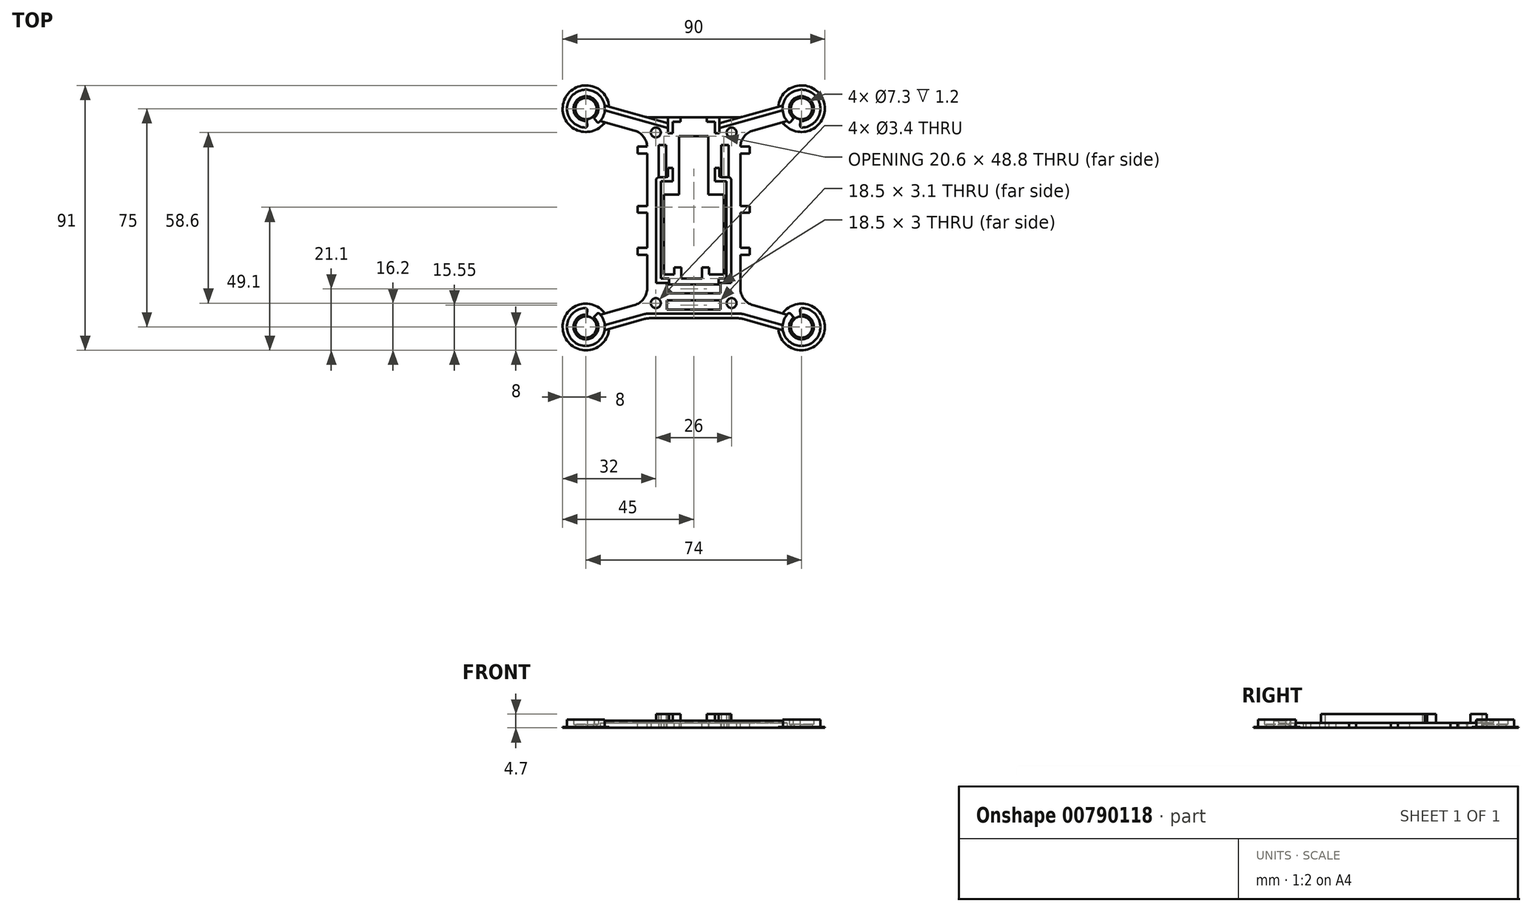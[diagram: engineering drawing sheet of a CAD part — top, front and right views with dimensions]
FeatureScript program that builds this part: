
annotation { "Feature Type Name" : "Feature", "Feature Type Description" : "" }
export const myFeature = defineFeature(function(context is Context, id is Id, definition is map)
    precondition{}
    {
        {
            var Q0;
            Q0=qCreatedBy(makeId("Top.planeOp"),FACE);
            var sketch = newSketch(context, id + "F0", { "sketchPlane" : qUnion([Q0])});
            skCircle(sketch, "E0", {"center": v(-37, 37.5) * mm, "radius": 32.5 * mm, "construction": true});
            skCircle(sketch, "E1.MirrorC", {"center": v(37, 37.5) * mm, "radius": 32.5 * mm, "construction": true});
            skCircle(sketch, "E2.MirrorC", {"center": v(37, -37.5) * mm, "radius": 32.5 * mm, "construction": true});
            skCircle(sketch, "E3.MirrorC", {"center": v(-37, -37.5) * mm, "radius": 32.5 * mm, "construction": true});
            skLineSegment(sketch, "E4.bottom", {"start": v(-37, 37.5) * mm, "end": v(37, 37.5) * mm, "construction": true});
            skLineSegment(sketch, "E4.top", {"start": v(-37, -37.5) * mm, "end": v(37, -37.5) * mm, "construction": true});
            skLineSegment(sketch, "E4.left", {"start": v(-37, 37.5) * mm, "end": v(-37, -37.5) * mm, "construction": true});
            skLineSegment(sketch, "E4.right", {"start": v(37, 37.5) * mm, "end": v(37, -37.5) * mm, "construction": true});
            skLineSegment(sketch, "E5", {"start": v(-37, 37.5) * mm, "end": v(0, 0) * mm, "construction": true});
            skCircle(sketch, "E6", {"center": v(-37, 37.5) * mm, "radius": 3.65 * mm});
            skCircle(sketch, "E7.MirrorC", {"center": v(37, 37.5) * mm, "radius": 3.65 * mm});
            skCircle(sketch, "E8.MirrorC", {"center": v(37, -37.5) * mm, "radius": 3.65 * mm});
            skCircle(sketch, "E9.MirrorC", {"center": v(-37, -37.5) * mm, "radius": 3.65 * mm});
            skArc(sketch, "E10", {"start": v(-30.59, 38.57) * mm, "mid": v(-43.26, 39.25) * mm, "end": v(-32.07, 33.27) * mm});
            skArc(sketch, "E11.MirrorC", {"start": v(30.59, 38.57) * mm, "mid": v(43.26, 39.25) * mm, "end": v(32.07, 33.27) * mm});
            skArc(sketch, "E12.MirrorC", {"start": v(-30.59, -38.57) * mm, "mid": v(-43.26, -39.25) * mm, "end": v(-32.07, -33.27) * mm});
            skArc(sketch, "E13.MirrorC", {"start": v(30.59, -38.57) * mm, "mid": v(43.26, -39.25) * mm, "end": v(32.07, -33.27) * mm});
            skLineSegment(sketch, "E14.bottom", {"start": v(-10.3, 11) * mm, "end": v(-5, 11) * mm, "construction": true});
            skLineSegment(sketch, "E14.top", {"start": v(-10.3, -20.5) * mm, "end": v(10.3, -20.5) * mm});
            skLineSegment(sketch, "E14.right", {"start": v(10.3, 8) * mm, "end": v(10.3, -20.5) * mm});
            skPoint(sketch, "E14.middle", {"position": v(0, -4.75) * mm});
            skLineSegment(sketch, "E15.top", {"start": v(-5, 28) * mm, "end": v(5, 28) * mm});
            skLineSegment(sketch, "E15.left", {"start": v(-5, 11) * mm, "end": v(-5, 16) * mm});
            skLineSegment(sketch, "E15.right", {"start": v(5, 11) * mm, "end": v(5, 16) * mm});
            skPoint(sketch, "E15.middle", {"position": v(0, 19.5) * mm});
            skPoint(sketch, "E15.middle.positionSnap0", {"position": v(0, 11) * mm});
            skPoint(sketch, "E15.centerSnap0", {"position": v(0, 11) * mm});
            skLineSegment(sketch, "E16.trimOffspring", {"start": v(5, 11) * mm, "end": v(10.3, 11) * mm, "construction": true});
            skLineSegment(sketch, "E17.bottom", {"start": v(-16, 34.5) * mm, "end": v(16, 34.5) * mm});
            skLineSegment(sketch, "E17.top", {"start": v(-16, -34.5) * mm, "end": v(16, -34.5) * mm});
            skLineSegment(sketch, "E17.left", {"start": v(-16, 28.8) * mm, "end": v(-16, -28.8) * mm});
            skLineSegment(sketch, "E17.right", {"start": v(16, 28.8) * mm, "end": v(16, -28.8) * mm});
            skPoint(sketch, "E17.middle", {"position": v(0, 0) * mm});
            skLineSegment(sketch, "E18", {"start": v(-30.59, 38.57) * mm, "end": v(-16, 34.5) * mm});
            skLineSegment(sketch, "E19", {"start": v(-32.07, 33.27) * mm, "end": v(-16, 28.8) * mm});
            skLineSegment(sketch, "E20", {"start": v(-37, 37.5) * mm, "end": v(-17.81, 32.15) * mm, "construction": true});
            skLineSegment(sketch, "E21.MirrorCS", {"start": v(30.59, 38.57) * mm, "end": v(16, 34.5) * mm});
            skLineSegment(sketch, "E22.MirrorCS", {"start": v(32.07, 33.27) * mm, "end": v(16, 28.8) * mm});
            skLineSegment(sketch, "E23.MirrorCS", {"start": v(-30.59, -38.57) * mm, "end": v(-16, -34.5) * mm});
            skLineSegment(sketch, "E24.MirrorCS", {"start": v(-32.07, -33.27) * mm, "end": v(-16, -28.8) * mm});
            skLineSegment(sketch, "E25.MirrorCS", {"start": v(30.59, -38.57) * mm, "end": v(16, -34.5) * mm});
            skLineSegment(sketch, "E26.MirrorCS", {"start": v(32.07, -33.27) * mm, "end": v(16, -28.8) * mm});
            skLineSegment(sketch, "E27.bottom", {"start": v(-11.3, 11.8) * mm, "end": v(11.3, 11.8) * mm, "construction": true});
            skLineSegment(sketch, "E27.top", {"start": v(-11.3, -21.3) * mm, "end": v(11.3, -21.3) * mm, "construction": true});
            skLineSegment(sketch, "E27.left", {"start": v(-11.3, 11.8) * mm, "end": v(-11.3, -21.3) * mm, "construction": true});
            skLineSegment(sketch, "E27.right", {"start": v(11.3, 11.8) * mm, "end": v(11.3, -21.3) * mm, "construction": true});
            skLineSegment(sketch, "E28.bottom", {"start": v(-9.25, -22.9) * mm, "end": v(9.25, -22.9) * mm});
            skLineSegment(sketch, "E28.top", {"start": v(-9.25, -25.9) * mm, "end": v(9.25, -25.9) * mm});
            skLineSegment(sketch, "E28.left", {"start": v(-9.25, -22.9) * mm, "end": v(-9.25, -25.9) * mm});
            skLineSegment(sketch, "E28.right", {"start": v(9.25, -22.9) * mm, "end": v(9.25, -25.9) * mm});
            skPoint(sketch, "E28.middle", {"position": v(0, -24.4) * mm});
            skLineSegment(sketch, "E29.bottom", {"start": v(-9.25, -28.4) * mm, "end": v(9.25, -28.4) * mm});
            skLineSegment(sketch, "E29.top", {"start": v(-9.25, -31.5) * mm, "end": v(9.25, -31.5) * mm});
            skLineSegment(sketch, "E29.left", {"start": v(-9.25, -28.4) * mm, "end": v(-9.25, -31.5) * mm});
            skLineSegment(sketch, "E29.right", {"start": v(9.25, -28.4) * mm, "end": v(9.25, -31.5) * mm});
            skPoint(sketch, "E29.middle", {"position": v(0, -29.95) * mm});
            skCircle(sketch, "E30", {"center": v(-13, 29.3) * mm, "radius": 1.7 * mm});
            skCircle(sketch, "E31.MirrorC", {"center": v(13, 29.3) * mm, "radius": 1.7 * mm});
            skCircle(sketch, "E32.MirrorC", {"center": v(-13, -29.3) * mm, "radius": 1.7 * mm});
            skCircle(sketch, "E33.MirrorC", {"center": v(13, -29.3) * mm, "radius": 1.7 * mm});
            skLineSegment(sketch, "E34.bottom", {"start": v(-12, 25) * mm, "end": v(-9.5, 25) * mm});
            skLineSegment(sketch, "E34.top", {"start": v(-12, 14) * mm, "end": v(-9.5, 14) * mm});
            skLineSegment(sketch, "E34.left", {"start": v(-12, 25) * mm, "end": v(-12, 14) * mm});
            skLineSegment(sketch, "E34.right", {"start": v(-9.5, 25) * mm, "end": v(-9.5, 14) * mm});
            skPoint(sketch, "E34.middle", {"position": v(-10.75, 19.5) * mm});
            skLineSegment(sketch, "E35.MirrorCS", {"start": v(12, 25) * mm, "end": v(9.5, 25) * mm});
            skLineSegment(sketch, "E36.MirrorCS", {"start": v(12, 25) * mm, "end": v(12, 14) * mm});
            skLineSegment(sketch, "E37.MirrorCS", {"start": v(12, 14) * mm, "end": v(9.5, 14) * mm});
            skLineSegment(sketch, "E38.MirrorCS", {"start": v(9.5, 25) * mm, "end": v(9.5, 14) * mm});
            skLineSegment(sketch, "E39.trimOffspring", {"start": v(-5, 16) * mm, "end": v(-5, 28) * mm});
            skLineSegment(sketch, "E40.trimOffspring", {"start": v(5, 16) * mm, "end": v(5, 28) * mm});
            skLineSegment(sketch, "E41", {"start": v(-10.3, 8) * mm, "end": v(-5, 8) * mm});
            skLineSegment(sketch, "E42", {"start": v(-5, 8) * mm, "end": v(-5, 11) * mm});
            skLineSegment(sketch, "E43.trimOffspring", {"start": v(-10.3, 8) * mm, "end": v(-10.3, -20.5) * mm});
            skLineSegment(sketch, "E44.MirrorCS", {"start": v(5, 8) * mm, "end": v(5, 11) * mm});
            skLineSegment(sketch, "E45.MirrorCS", {"start": v(10.3, 8) * mm, "end": v(5, 8) * mm});
            skSolve(sketch);
        }
        {
            var Q0;
            Q0=makeQuery(id+"F0.imprint","IMPRINT",FACE,{"disambiguationData":[TD([[makeQuery(id+"F0.imprint","IMPRINT",EDGE,{"derivedFrom":sQuery(id+"F0.wireOp",EDGE,"E6")}),-1.0]])]});
            extrude(context, id + "F1", {"entities" : qUnion([Q0]), "depth" : 1.7 * mm, "offsetDistance" : 25 * mm});
        }
        {
            var Q0;
            Q0=makeQuery(id+"F1.opExtrude","CAP_FACE",FACE,{"disambiguationData":[OSD([sQuery(id+"F0.wireOp",EDGE,"E6"),sQuery(id+"F0.wireOp",EDGE,"E7.MirrorC"),sQuery(id+"F0.wireOp",EDGE,"E8.MirrorC"),sQuery(id+"F0.wireOp",EDGE,"E9.MirrorC"),sQuery(id+"F0.wireOp",EDGE,"E10"),sQuery(id+"F0.wireOp",EDGE,"E11.MirrorC"),sQuery(id+"F0.wireOp",EDGE,"E12.MirrorC"),sQuery(id+"F0.wireOp",EDGE,"E13.MirrorC"),sQuery(id+"F0.wireOp",EDGE,"E14.bottom"),sQuery(id+"F0.wireOp",EDGE,"E14.top"),sQuery(id+"F0.wireOp",EDGE,"E14.left"),sQuery(id+"F0.wireOp",EDGE,"E14.right"),sQuery(id+"F0.wireOp",EDGE,"E15.top"),sQuery(id+"F0.wireOp",EDGE,"E15.left"),sQuery(id+"F0.wireOp",EDGE,"E15.right"),sQuery(id+"F0.wireOp",EDGE,"E16.trimOffspring"),sQuery(id+"F0.wireOp",EDGE,"E17.bottom"),sQuery(id+"F0.wireOp",EDGE,"E17.top"),sQuery(id+"F0.wireOp",EDGE,"E17.left"),sQuery(id+"F0.wireOp",EDGE,"E17.right"),sQuery(id+"F0.wireOp",EDGE,"E18"),sQuery(id+"F0.wireOp",EDGE,"E19"),sQuery(id+"F0.wireOp",EDGE,"E21.MirrorCS"),sQuery(id+"F0.wireOp",EDGE,"E22.MirrorCS"),sQuery(id+"F0.wireOp",EDGE,"E23.MirrorCS"),sQuery(id+"F0.wireOp",EDGE,"E24.MirrorCS"),sQuery(id+"F0.wireOp",EDGE,"E25.MirrorCS"),sQuery(id+"F0.wireOp",EDGE,"E26.MirrorCS")])],"isStart":false});
            var sketch = newSketch(context, id + "F2", { "sketchPlane" : qUnion([Q0])});
            skLineSegment(sketch, "E46.bottom", {"start": v(-11.25, 12.5) * mm, "end": v(-7.25, 12.5) * mm});
            skLineSegment(sketch, "E46.top", {"start": v(-11.25, -20.8) * mm, "end": v(11.25, -20.8) * mm});
            skLineSegment(sketch, "E46.left", {"start": v(-11.25, 12.5) * mm, "end": v(-11.25, -20.8) * mm});
            skLineSegment(sketch, "E46.right", {"start": v(11.25, 12.5) * mm, "end": v(11.25, -20.8) * mm});
            skPoint(sketch, "E46.middle", {"position": v(0, -4.15) * mm});
            skLineSegment(sketch, "E47.bottom", {"start": v(-12.85, 14.1) * mm, "end": v(-8.85, 14.1) * mm});
            skLineSegment(sketch, "E47.top", {"start": v(-12.85, -22.4) * mm, "end": v(12.85, -22.4) * mm});
            skLineSegment(sketch, "E47.left", {"start": v(-12.85, 14.1) * mm, "end": v(-12.85, -22.4) * mm});
            skLineSegment(sketch, "E47.right", {"start": v(12.85, 14.1) * mm, "end": v(12.85, -22.4) * mm});
            skLineSegment(sketch, "E48", {"start": v(-7.25, 14.1) * mm, "end": v(-7.25, 33) * mm});
            skLineSegment(sketch, "E49", {"start": v(-7.25, 33) * mm, "end": v(7.25, 33) * mm});
            skLineSegment(sketch, "E50", {"start": v(7.25, 33) * mm, "end": v(7.25, 14.1) * mm});
            skLineSegment(sketch, "E51", {"start": v(-8.85, 14.1) * mm, "end": v(-8.85, 34.6) * mm});
            skLineSegment(sketch, "E52", {"start": v(-8.85, 34.6) * mm, "end": v(8.85, 34.6) * mm});
            skLineSegment(sketch, "E53", {"start": v(8.85, 34.6) * mm, "end": v(8.85, 14.1) * mm});
            skLineSegment(sketch, "E54.trimOffspring", {"start": v(8.85, 14.1) * mm, "end": v(12.85, 14.1) * mm});
            skLineSegment(sketch, "E55", {"start": v(-7.25, 14.1) * mm, "end": v(-7.25, 12.5) * mm});
            skLineSegment(sketch, "E56", {"start": v(7.25, 14.1) * mm, "end": v(7.25, 12.5) * mm});
            skLineSegment(sketch, "E57.trimOffspring", {"start": v(7.25, 12.5) * mm, "end": v(11.25, 12.5) * mm});
            skSolve(sketch);
        }
        {
            var Q0;
            Q0=makeQuery(id+"F2.imprint","IMPRINT",FACE,{"disambiguationData":[TD([[makeQuery(id+"F2.imprint","IMPRINT",EDGE,{"derivedFrom":sQuery(id+"F2.wireOp",EDGE,"E46.bottom")}),1.0]])]});
            extrude(context, id + "F3", {"entities" : qUnion([Q0]), "operationType" : NewBodyOperationType.ADD, "depth" : 3 * mm, "offsetDistance" : 25 * mm});
        }
        {
            var Q0;
            Q0=makeQuery(id+"F3.opExtrude","SWEPT_EDGE",EDGE,{"disambiguationData":[OSD([sQuery(id+"F2.wireOp",EDGE,"E47.bottom"),sQuery(id+"F2.wireOp",EDGE,"E47.left")])]});
            var Q1;
            Q1=makeQuery(id+"F3.opExtrude","SWEPT_EDGE",EDGE,{"disambiguationData":[OSD([sQuery(id+"F2.wireOp",EDGE,"E47.right"),sQuery(id+"F2.wireOp",EDGE,"E54.trimOffspring")])]});
            chamfer(context, id + "F4", {"entities" : qUnion([Q0, Q1]), "width" : 0.8 * mm, "tangentPropagation" : true});
        }
        {
            var Q0;
            Q0=makeQuery(id+"F3.opExtrude","CAP_FACE",FACE,{"disambiguationData":[OSD([sQuery(id+"F2.wireOp",EDGE,"E46.bottom"),sQuery(id+"F2.wireOp",EDGE,"E46.top"),sQuery(id+"F2.wireOp",EDGE,"E46.left"),sQuery(id+"F2.wireOp",EDGE,"E46.right"),sQuery(id+"F2.wireOp",EDGE,"E47.bottom"),sQuery(id+"F2.wireOp",EDGE,"E47.top"),sQuery(id+"F2.wireOp",EDGE,"E47.left"),sQuery(id+"F2.wireOp",EDGE,"E47.right"),sQuery(id+"F2.wireOp",EDGE,"E48"),sQuery(id+"F2.wireOp",EDGE,"E49"),sQuery(id+"F2.wireOp",EDGE,"E50"),sQuery(id+"F2.wireOp",EDGE,"E51"),sQuery(id+"F2.wireOp",EDGE,"E52"),sQuery(id+"F2.wireOp",EDGE,"E53"),sQuery(id+"F2.wireOp",EDGE,"E54.trimOffspring"),sQuery(id+"F2.wireOp",EDGE,"E55"),sQuery(id+"F2.wireOp",EDGE,"E56"),sQuery(id+"F2.wireOp",EDGE,"E57.trimOffspring")])],"isStart":false});
            var sketch = newSketch(context, id + "F5", { "sketchPlane" : qUnion([Q0])});
            skLineSegment(sketch, "E58.bottom", {"start": v(-4.5, 34.5) * mm, "end": v(4.5, 34.5) * mm});
            skLineSegment(sketch, "E58.top", {"start": v(-4.5, 33) * mm, "end": v(4.5, 33) * mm});
            skLineSegment(sketch, "E58.left", {"start": v(-4.5, 34.5) * mm, "end": v(-4.5, 33) * mm});
            skLineSegment(sketch, "E58.right", {"start": v(4.5, 34.5) * mm, "end": v(4.5, 33) * mm});
            skPoint(sketch, "E58.middle", {"position": v(0, 33.75) * mm});
            skLineSegment(sketch, "E59.bottom", {"start": v(-8.5, -20.8) * mm, "end": v(8.5, -20.8) * mm});
            skLineSegment(sketch, "E59.top", {"start": v(-8.5, -22.4) * mm, "end": v(8.5, -22.4) * mm});
            skLineSegment(sketch, "E59.left", {"start": v(-8.5, -20.8) * mm, "end": v(-8.5, -22.4) * mm});
            skLineSegment(sketch, "E59.right", {"start": v(8.5, -20.8) * mm, "end": v(8.5, -22.4) * mm});
            skPoint(sketch, "E59.middle", {"position": v(0, -21.6) * mm});
            skLineSegment(sketch, "E60.bottom", {"start": v(-8.85, 29) * mm, "end": v(-7.25, 29) * mm});
            skLineSegment(sketch, "E60.top", {"start": v(-8.85, 17.1) * mm, "end": v(-7.25, 17.1) * mm});
            skLineSegment(sketch, "E60.left", {"start": v(-8.85, 29) * mm, "end": v(-8.85, 17.1) * mm});
            skLineSegment(sketch, "E60.right", {"start": v(-7.25, 29) * mm, "end": v(-7.25, 17.1) * mm});
            skLineSegment(sketch, "E61.MirrorCS", {"start": v(8.85, 29) * mm, "end": v(7.25, 29) * mm});
            skLineSegment(sketch, "E62.MirrorCS", {"start": v(8.85, 17.1) * mm, "end": v(7.25, 17.1) * mm});
            skLineSegment(sketch, "E63.MirrorCS", {"start": v(7.25, 29) * mm, "end": v(7.25, 17.1) * mm});
            skLineSegment(sketch, "E64.MirrorCS", {"start": v(8.85, 29) * mm, "end": v(8.85, 17.1) * mm});
            skSolve(sketch);
        }
        {
            var Q0;
            Q0 = qSketchRegion(id + "F5", true);
            var Q1;
            {var subQ0=sQuery(id+"F0.wireOp",EDGE,"E38.MirrorCS");var subQ1=sQuery(id+"F0.wireOp",EDGE,"E37.MirrorCS");var subQ2=sQuery(id+"F0.wireOp",EDGE,"E36.MirrorCS");var subQ3=sQuery(id+"F0.wireOp",EDGE,"E35.MirrorCS");var subQ4=sQuery(id+"F0.wireOp",EDGE,"E29.top");var subQ5=sQuery(id+"F0.wireOp",EDGE,"E34.right");var subQ6=sQuery(id+"F0.wireOp",EDGE,"E29.bottom");var subQ7=sQuery(id+"F0.wireOp",EDGE,"E34.left");var subQ8=sQuery(id+"F0.wireOp",EDGE,"E34.top");var subQ9=sQuery(id+"F0.wireOp",EDGE,"E34.bottom");var subQ10=sQuery(id+"F0.wireOp",EDGE,"E33.MirrorC");var subQ11=sQuery(id+"F0.wireOp",EDGE,"E28.bottom");var subQ12=sQuery(id+"F0.wireOp",EDGE,"E32.MirrorC");var subQ13=sQuery(id+"F0.wireOp",EDGE,"E26.MirrorCS");var subQ14=sQuery(id+"F0.wireOp",EDGE,"E31.MirrorC");var subQ15=sQuery(id+"F0.wireOp",EDGE,"E25.MirrorCS");var subQ16=sQuery(id+"F0.wireOp",EDGE,"E30");var subQ17=sQuery(id+"F0.wireOp",EDGE,"E24.MirrorCS");var subQ18=sQuery(id+"F0.wireOp",EDGE,"E29.right");var subQ19=sQuery(id+"F0.wireOp",EDGE,"E29.left");var subQ20=sQuery(id+"F0.wireOp",EDGE,"E28.right");var subQ21=sQuery(id+"F0.wireOp",EDGE,"E28.left");var subQ22=sQuery(id+"F0.wireOp",EDGE,"E13.MirrorC");var subQ23=sQuery(id+"F0.wireOp",EDGE,"E12.MirrorC");var subQ24=sQuery(id+"F0.wireOp",EDGE,"E11.MirrorC");var subQ25=sQuery(id+"F0.wireOp",EDGE,"E10");var subQ26=sQuery(id+"F0.wireOp",EDGE,"E6");var subQ27=sQuery(id+"F0.wireOp",EDGE,"E23.MirrorCS");var subQ28=sQuery(id+"F0.wireOp",EDGE,"E17.top");var subQ29=sQuery(id+"F0.wireOp",EDGE,"E9.MirrorC");var subQ30=sQuery(id+"F0.wireOp",EDGE,"E28.top");var subQ31=sQuery(id+"F0.wireOp",EDGE,"E7.MirrorC");var subQ32=sQuery(id+"F0.wireOp",EDGE,"E17.bottom");var subQ33=sQuery(id+"F0.wireOp",EDGE,"E8.MirrorC");var subQ34=sQuery(id+"F0.wireOp",EDGE,"E17.left");var subQ35=sQuery(id+"F0.wireOp",EDGE,"E17.right");var subQ36=sQuery(id+"F0.wireOp",EDGE,"E18");var subQ37=sQuery(id+"F0.wireOp",EDGE,"E19");var subQ38=sQuery(id+"F0.wireOp",EDGE,"E21.MirrorCS");var subQ39=sQuery(id+"F0.wireOp",EDGE,"E22.MirrorCS");Q1=makeQuery(id+"F3.boolean.opBoolean","SPLIT",FACE,{"disambiguationData":[TD([makeQuery(id+"F1.opExtrude","SWEPT_FACE",FACE,{"disambiguationData":[OSD([subQ26])]})])],"derivedFrom":makeQuery(id+"F1.opExtrude","CAP_FACE",FACE,{"disambiguationData":[OSD([subQ26,subQ31,subQ33,subQ29,subQ25,subQ24,subQ23,subQ22,sQuery(id+"F0.wireOp",EDGE,"E14.top"),sQuery(id+"F0.wireOp",EDGE,"E14.right"),sQuery(id+"F0.wireOp",EDGE,"E15.top"),sQuery(id+"F0.wireOp",EDGE,"E15.left"),sQuery(id+"F0.wireOp",EDGE,"E15.right"),subQ32,subQ28,subQ34,subQ35,subQ36,subQ37,subQ38,subQ39,subQ27,subQ17,subQ15,subQ13,subQ11,subQ30,subQ21,subQ20,subQ6,subQ4,subQ19,subQ18,subQ16,subQ14,subQ12,subQ10,subQ9,subQ8,subQ7,subQ5,subQ3,subQ2,subQ1,subQ0,sQuery(id+"F0.wireOp",EDGE,"E39.trimOffspring"),sQuery(id+"F0.wireOp",EDGE,"E40.trimOffspring"),sQuery(id+"F0.wireOp",EDGE,"E41"),sQuery(id+"F0.wireOp",EDGE,"E42"),sQuery(id+"F0.wireOp",EDGE,"E43.trimOffspring"),sQuery(id+"F0.wireOp",EDGE,"E44.MirrorCS"),sQuery(id+"F0.wireOp",EDGE,"E45.MirrorCS")])],"isStart":false})});}
            extrude(context, id + "F6", {"entities" : qUnion([Q0]), "operationType" : NewBodyOperationType.REMOVE, "endBound" : BoundingType.UP_TO_SURFACE, "oppositeDirection" : true, "depth" : 25 * mm, "endBoundEntityFace" : qUnion([Q1]), "offsetDistance" : 25 * mm});
        }
        {
            var Q0;
            {var subQ26=sQuery(id+"F0.wireOp",EDGE,"E14.top");Q0=makeQuery(id+"FuSGAjuN3hY24FW_1.boolean.opBoolean","SPLIT",FACE,{"disambiguationData":[TD([makeQuery(id+"FuSGAjuN3hY24FW_1.opExtrude","SWEPT_FACE",FACE,{"disambiguationData":[OSD([sQuery(id+"FYQ8BpSlA4rBM08_1.wireOp",EDGE,"MOxF5YxK-4EZ1-Xr4a-WxPD-GJG52SWqdB7U")])]})])],"derivedFrom":makeQuery(id+"F1.opExtrude","SWEPT_FACE",FACE,{"disambiguationData":[OSD([subQ26])]})});}
            var Q1;
            {var subQ26=sQuery(id+"F0.wireOp",EDGE,"E14.top");Q1=makeQuery(id+"FuSGAjuN3hY24FW_1.boolean.opBoolean","SPLIT",FACE,{"disambiguationData":[TD([makeQuery(id+"FuSGAjuN3hY24FW_1.opExtrude","SWEPT_FACE",FACE,{"disambiguationData":[OSD([sQuery(id+"FYQ8BpSlA4rBM08_1.wireOp",EDGE,"8e189bec-98aa-4e8d-a065-43acc68c2a770.MirrorCS")])]})])],"derivedFrom":makeQuery(id+"F1.opExtrude","SWEPT_FACE",FACE,{"disambiguationData":[OSD([subQ26])]})});}
            extrude(context, id + "F7", {"entities" : qUnion([Q0, Q1]), "operationType" : NewBodyOperationType.ADD, "depth" : 1 * mm, "offsetDistance" : 25 * mm});
        }
        {
            var Q0;
            {var subQ0=sQuery(id+"F0.wireOp",EDGE,"E22.MirrorCS");var subQ1=sQuery(id+"F0.wireOp",EDGE,"E21.MirrorCS");var subQ2=sQuery(id+"F0.wireOp",EDGE,"E18");var subQ3=sQuery(id+"F0.wireOp",EDGE,"E17.right");var subQ4=sQuery(id+"F0.wireOp",EDGE,"E17.left");var subQ5=sQuery(id+"F0.wireOp",EDGE,"E24.MirrorCS");var subQ6=sQuery(id+"F0.wireOp",EDGE,"E8.MirrorC");var subQ7=sQuery(id+"F0.wireOp",EDGE,"E23.MirrorCS");var subQ8=sQuery(id+"F0.wireOp",EDGE,"E7.MirrorC");var subQ9=sQuery(id+"F0.wireOp",EDGE,"E25.MirrorCS");var subQ10=sQuery(id+"F0.wireOp",EDGE,"E9.MirrorC");var subQ11=sQuery(id+"F0.wireOp",EDGE,"E19");var subQ12=sQuery(id+"F0.wireOp",EDGE,"E6");var subQ13=sQuery(id+"F0.wireOp",EDGE,"E26.MirrorCS");var subQ14=sQuery(id+"F0.wireOp",EDGE,"E10");var subQ15=sQuery(id+"F0.wireOp",EDGE,"E28.bottom");var subQ16=sQuery(id+"F0.wireOp",EDGE,"E11.MirrorC");var subQ17=sQuery(id+"F0.wireOp",EDGE,"E17.bottom");var subQ18=sQuery(id+"F0.wireOp",EDGE,"E28.top");var subQ19=sQuery(id+"F0.wireOp",EDGE,"E12.MirrorC");var subQ20=sQuery(id+"F0.wireOp",EDGE,"E17.top");var subQ21=sQuery(id+"F0.wireOp",EDGE,"E13.MirrorC");var subQ22=sQuery(id+"F0.wireOp",EDGE,"E28.left");var subQ23=sQuery(id+"F0.wireOp",EDGE,"E28.right");var subQ24=sQuery(id+"F0.wireOp",EDGE,"E29.bottom");var subQ25=sQuery(id+"F0.wireOp",EDGE,"E29.top");var subQ26=sQuery(id+"F0.wireOp",EDGE,"E29.left");var subQ27=sQuery(id+"F0.wireOp",EDGE,"E29.right");var subQ28=sQuery(id+"F0.wireOp",EDGE,"E30");var subQ29=sQuery(id+"F0.wireOp",EDGE,"E31.MirrorC");var subQ30=sQuery(id+"F0.wireOp",EDGE,"E32.MirrorC");var subQ31=sQuery(id+"F0.wireOp",EDGE,"E33.MirrorC");var subQ32=sQuery(id+"F0.wireOp",EDGE,"LB6rmxyj-JH5l-yOl6-IWSN-3rPoN5P4rQFK");var subQ33=sQuery(id+"F0.wireOp",EDGE,"e03a44ee-9eac-46e1-b4e1-07f127c7162c0.MirrorC");Q0=makeQuery(id+"F3.boolean.opBoolean","SPLIT",FACE,{"disambiguationData":[TD([makeQuery(id+"F1.opExtrude","SWEPT_FACE",FACE,{"disambiguationData":[OSD([subQ12])]})])],"derivedFrom":makeQuery(id+"F1.opExtrude","CAP_FACE",FACE,{"disambiguationData":[OSD([subQ12,subQ8,subQ6,subQ10,subQ14,subQ16,subQ19,subQ21,sQuery(id+"F0.wireOp",EDGE,"E14.bottom"),sQuery(id+"F0.wireOp",EDGE,"E14.top"),sQuery(id+"F0.wireOp",EDGE,"E14.left"),sQuery(id+"F0.wireOp",EDGE,"E14.right"),sQuery(id+"F0.wireOp",EDGE,"E15.top"),sQuery(id+"F0.wireOp",EDGE,"E15.left"),sQuery(id+"F0.wireOp",EDGE,"E15.right"),sQuery(id+"F0.wireOp",EDGE,"E16.trimOffspring"),subQ17,subQ20,subQ4,subQ3,subQ2,subQ11,subQ1,subQ0,subQ7,subQ5,subQ9,subQ13,subQ15,subQ18,subQ22,subQ23,subQ24,subQ25,subQ26,subQ27,subQ28,subQ29,subQ30,subQ31,subQ32,subQ33])],"isStart":false})});}
            var sketch = newSketch(context, id + "F8", { "sketchPlane" : qUnion([Q0])});
            skCircle(sketch, "E65", {"center": v(-37, 37.5) * mm, "radius": 4.25 * mm});
            skCircle(sketch, "E66", {"center": v(-37, 37.5) * mm, "radius": 6.5 * mm});
            skCircle(sketch, "E67.MirrorC", {"center": v(37, 37.5) * mm, "radius": 4.25 * mm});
            skCircle(sketch, "E68.MirrorC", {"center": v(37, 37.5) * mm, "radius": 6.5 * mm});
            skCircle(sketch, "E69.MirrorC", {"center": v(-37, -37.5) * mm, "radius": 6.5 * mm});
            skCircle(sketch, "E70.MirrorC", {"center": v(-37, -37.5) * mm, "radius": 4.25 * mm});
            skCircle(sketch, "E71.MirrorC", {"center": v(37, -37.5) * mm, "radius": 6.5 * mm});
            skCircle(sketch, "E72.MirrorC", {"center": v(37, -37.5) * mm, "radius": 4.25 * mm});
            skSolve(sketch);
        }
        {
            var Q0;
            Q0 = qSketchRegion(id + "F8", true);
            extrude(context, id + "F9", {"entities" : qUnion([Q0]), "operationType" : NewBodyOperationType.ADD, "depth" : 1.2 * mm, "offsetDistance" : 25 * mm});
        }
        {
            var Q0;
            Q0=makeQuery(id+"F1.opExtrude","SWEPT_EDGE",EDGE,{"disambiguationData":[OSD([sQuery(id+"F0.wireOp",EDGE,"E17.left"),sQuery(id+"F0.wireOp",EDGE,"E19")])]});
            var Q1;
            Q1=makeQuery(id+"F1.opExtrude","SWEPT_EDGE",EDGE,{"disambiguationData":[OSD([sQuery(id+"F0.wireOp",EDGE,"E17.left"),sQuery(id+"F0.wireOp",EDGE,"E24.MirrorCS")])]});
            var Q2;
            Q2=makeQuery(id+"F1.opExtrude","SWEPT_EDGE",EDGE,{"disambiguationData":[OSD([sQuery(id+"F0.wireOp",EDGE,"E17.bottom"),sQuery(id+"F0.wireOp",EDGE,"E21.MirrorCS")])]});
            var Q3;
            Q3=makeQuery(id+"F1.opExtrude","SWEPT_EDGE",EDGE,{"disambiguationData":[OSD([sQuery(id+"F0.wireOp",EDGE,"E17.bottom"),sQuery(id+"F0.wireOp",EDGE,"E18")])]});
            var Q4;
            Q4=makeQuery(id+"F1.opExtrude","SWEPT_EDGE",EDGE,{"disambiguationData":[OSD([sQuery(id+"F0.wireOp",EDGE,"E17.right"),sQuery(id+"F0.wireOp",EDGE,"E22.MirrorCS")])]});
            var Q5;
            Q5=makeQuery(id+"F1.opExtrude","SWEPT_EDGE",EDGE,{"disambiguationData":[OSD([sQuery(id+"F0.wireOp",EDGE,"E17.right"),sQuery(id+"F0.wireOp",EDGE,"E26.MirrorCS")])]});
            var Q6;
            Q6=makeQuery(id+"F1.opExtrude","SWEPT_EDGE",EDGE,{"disambiguationData":[OSD([sQuery(id+"F0.wireOp",EDGE,"E17.top"),sQuery(id+"F0.wireOp",EDGE,"E25.MirrorCS")])]});
            var Q7;
            Q7=makeQuery(id+"F1.opExtrude","SWEPT_EDGE",EDGE,{"disambiguationData":[OSD([sQuery(id+"F0.wireOp",EDGE,"E17.top"),sQuery(id+"F0.wireOp",EDGE,"E23.MirrorCS")])]});
            fillet(context, id + "F10", {"entities" : qUnion([Q0, Q1, Q2, Q3, Q4, Q5, Q6, Q7]), "radius" : 6 * mm, "tangentPropagation" : true, "allowEdgeOverflow" : false});
        }
        {
            var Q0;
            Q0=makeQuery(id+"F9.opExtrude","CAP_FACE",FACE,{"disambiguationData":[OSD([sQuery(id+"F8.wireOp",EDGE,"E69.MirrorC"),sQuery(id+"F8.wireOp",EDGE,"E70.MirrorC")])],"isStart":false});
            var sketch = newSketch(context, id + "F11", { "sketchPlane" : qUnion([Q0])});
            skLineSegment(sketch, "E73", {"start": v(-37, -37.5) * mm, "end": v(-31.33, -23.4) * mm, "construction": true});
            skLineSegment(sketch, "E74", {"start": v(-37, -37.5) * mm, "end": v(-36.24, -27.73) * mm});
            skLineSegment(sketch, "E75", {"start": v(-36.24, -27.73) * mm, "end": v(-30.78, -29.93) * mm});
            skLineSegment(sketch, "E76", {"start": v(-30.78, -29.93) * mm, "end": v(-37, -37.5) * mm});
            skLineSegment(sketch, "E77.MirrorCS", {"start": v(36.24, -27.73) * mm, "end": v(30.78, -29.93) * mm});
            skLineSegment(sketch, "E78.MirrorCS", {"start": v(30.78, -29.93) * mm, "end": v(37, -37.5) * mm});
            skLineSegment(sketch, "E79.MirrorCS", {"start": v(37, -37.5) * mm, "end": v(31.33, -23.4) * mm, "construction": true});
            skLineSegment(sketch, "E80.MirrorCS", {"start": v(37, -37.5) * mm, "end": v(36.24, -27.73) * mm});
            skLineSegment(sketch, "E81.MirrorCS", {"start": v(-36.24, 27.73) * mm, "end": v(-30.78, 29.93) * mm});
            skLineSegment(sketch, "E82.MirrorCS", {"start": v(30.78, 29.93) * mm, "end": v(37, 37.5) * mm});
            skLineSegment(sketch, "E83.MirrorCS", {"start": v(37, 37.5) * mm, "end": v(31.33, 23.4) * mm, "construction": true});
            skLineSegment(sketch, "E84.MirrorCS", {"start": v(-37, 37.5) * mm, "end": v(-31.33, 23.4) * mm, "construction": true});
            skLineSegment(sketch, "E85.MirrorCS", {"start": v(-37, 37.5) * mm, "end": v(-36.24, 27.73) * mm});
            skLineSegment(sketch, "E86.MirrorCS", {"start": v(36.24, 27.73) * mm, "end": v(30.78, 29.93) * mm});
            skLineSegment(sketch, "E87.MirrorCS", {"start": v(-30.78, 29.93) * mm, "end": v(-37, 37.5) * mm});
            skLineSegment(sketch, "E88.MirrorCS", {"start": v(37, 37.5) * mm, "end": v(36.24, 27.73) * mm});
            skSolve(sketch);
        }
        {
            var Q0;
            Q0 = qSketchRegion(id + "F11", true);
            extrude(context, id + "F12", {"entities" : qUnion([Q0]), "operationType" : NewBodyOperationType.REMOVE, "oppositeDirection" : true, "depth" : 25 * mm, "offsetDistance" : 25 * mm});
        }
        {
            var Q0;
            Q0=makeQuery(id+"F12.boolean.opBoolean","INTERSECT",EDGE,{"derivedFrom":[makeQuery(id+"F9.boolean.opBoolean","MERGE",FACE,{"derivedFrom":[makeQuery(id+"F1.opExtrude","SWEPT_FACE",FACE,{"disambiguationData":[OSD([sQuery(id+"F0.wireOp",EDGE,"E10")])]}),makeQuery(id+"F9.opExtrude","SWEPT_FACE",FACE,{"disambiguationData":[OSD([sQuery(id+"F8.wireOp",EDGE,"E66")])]})]}),makeQuery(id+"F12.opExtrude","SWEPT_FACE",FACE,{"disambiguationData":[OSD([sQuery(id+"F11.wireOp",EDGE,"E85.MirrorCS")])]})]});
            var Q1;
            Q1=makeQuery(id+"F12.boolean.opBoolean","INTERSECT",EDGE,{"derivedFrom":[makeQuery(id+"F9.opExtrude","SWEPT_FACE",FACE,{"disambiguationData":[OSD([sQuery(id+"F8.wireOp",EDGE,"E65")])]}),makeQuery(id+"F12.opExtrude","SWEPT_FACE",FACE,{"disambiguationData":[OSD([sQuery(id+"F11.wireOp",EDGE,"E85.MirrorCS")])]})]});
            var Q2;
            Q2=makeQuery(id+"F12.boolean.opBoolean","INTERSECT",EDGE,{"derivedFrom":[makeQuery(id+"F1.opExtrude","SWEPT_FACE",FACE,{"disambiguationData":[OSD([sQuery(id+"F0.wireOp",EDGE,"E6")])]}),makeQuery(id+"F12.opExtrude","SWEPT_FACE",FACE,{"disambiguationData":[OSD([sQuery(id+"F11.wireOp",EDGE,"E85.MirrorCS")])]})]});
            var Q3;
            Q3=makeQuery(id+"F12.boolean.opBoolean","INTERSECT",EDGE,{"derivedFrom":[makeQuery(id+"F1.opExtrude","SWEPT_FACE",FACE,{"disambiguationData":[OSD([sQuery(id+"F0.wireOp",EDGE,"E6")])]}),makeQuery(id+"F12.opExtrude","SWEPT_FACE",FACE,{"disambiguationData":[OSD([sQuery(id+"F11.wireOp",EDGE,"E87.MirrorCS")])]})]});
            var Q4;
            Q4=makeQuery(id+"F12.boolean.opBoolean","INTERSECT",EDGE,{"derivedFrom":[makeQuery(id+"F9.boolean.opBoolean","MERGE",FACE,{"derivedFrom":[makeQuery(id+"F1.opExtrude","SWEPT_FACE",FACE,{"disambiguationData":[OSD([sQuery(id+"F0.wireOp",EDGE,"E10")])]}),makeQuery(id+"F9.opExtrude","SWEPT_FACE",FACE,{"disambiguationData":[OSD([sQuery(id+"F8.wireOp",EDGE,"E66")])]})]}),makeQuery(id+"F12.opExtrude","SWEPT_FACE",FACE,{"disambiguationData":[OSD([sQuery(id+"F11.wireOp",EDGE,"E87.MirrorCS")])]})]});
            var Q5;
            Q5=makeQuery(id+"F12.boolean.opBoolean","INTERSECT",EDGE,{"derivedFrom":[makeQuery(id+"F9.boolean.opBoolean","MERGE",FACE,{"derivedFrom":[makeQuery(id+"F1.opExtrude","SWEPT_FACE",FACE,{"disambiguationData":[OSD([sQuery(id+"F0.wireOp",EDGE,"E11.MirrorC")])]}),makeQuery(id+"F9.opExtrude","SWEPT_FACE",FACE,{"disambiguationData":[OSD([sQuery(id+"F8.wireOp",EDGE,"E68.MirrorC")])]})]}),makeQuery(id+"F12.opExtrude","SWEPT_FACE",FACE,{"disambiguationData":[OSD([sQuery(id+"F11.wireOp",EDGE,"E82.MirrorCS")])]})]});
            var Q6;
            Q6=makeQuery(id+"F12.boolean.opBoolean","INTERSECT",EDGE,{"derivedFrom":[makeQuery(id+"F9.opExtrude","SWEPT_FACE",FACE,{"disambiguationData":[OSD([sQuery(id+"F8.wireOp",EDGE,"E67.MirrorC")])]}),makeQuery(id+"F12.opExtrude","SWEPT_FACE",FACE,{"disambiguationData":[OSD([sQuery(id+"F11.wireOp",EDGE,"E82.MirrorCS")])]})]});
            var Q7;
            Q7=makeQuery(id+"F12.boolean.opBoolean","INTERSECT",EDGE,{"derivedFrom":[makeQuery(id+"F1.opExtrude","SWEPT_FACE",FACE,{"disambiguationData":[OSD([sQuery(id+"F0.wireOp",EDGE,"E7.MirrorC")])]}),makeQuery(id+"F12.opExtrude","SWEPT_FACE",FACE,{"disambiguationData":[OSD([sQuery(id+"F11.wireOp",EDGE,"E82.MirrorCS")])]})]});
            var Q8;
            Q8=makeQuery(id+"F12.boolean.opBoolean","INTERSECT",EDGE,{"derivedFrom":[makeQuery(id+"F9.boolean.opBoolean","MERGE",FACE,{"derivedFrom":[makeQuery(id+"F1.opExtrude","SWEPT_FACE",FACE,{"disambiguationData":[OSD([sQuery(id+"F0.wireOp",EDGE,"E11.MirrorC")])]}),makeQuery(id+"F9.opExtrude","SWEPT_FACE",FACE,{"disambiguationData":[OSD([sQuery(id+"F8.wireOp",EDGE,"E68.MirrorC")])]})]}),makeQuery(id+"F12.opExtrude","SWEPT_FACE",FACE,{"disambiguationData":[OSD([sQuery(id+"F11.wireOp",EDGE,"E88.MirrorCS")])]})]});
            var Q9;
            Q9=makeQuery(id+"F12.boolean.opBoolean","INTERSECT",EDGE,{"derivedFrom":[makeQuery(id+"F9.opExtrude","SWEPT_FACE",FACE,{"disambiguationData":[OSD([sQuery(id+"F8.wireOp",EDGE,"E67.MirrorC")])]}),makeQuery(id+"F12.opExtrude","SWEPT_FACE",FACE,{"disambiguationData":[OSD([sQuery(id+"F11.wireOp",EDGE,"E88.MirrorCS")])]})]});
            var Q10;
            Q10=makeQuery(id+"F12.boolean.opBoolean","INTERSECT",EDGE,{"derivedFrom":[makeQuery(id+"F1.opExtrude","SWEPT_FACE",FACE,{"disambiguationData":[OSD([sQuery(id+"F0.wireOp",EDGE,"E7.MirrorC")])]}),makeQuery(id+"F12.opExtrude","SWEPT_FACE",FACE,{"disambiguationData":[OSD([sQuery(id+"F11.wireOp",EDGE,"E88.MirrorCS")])]})]});
            var Q11;
            Q11=makeQuery(id+"F12.boolean.opBoolean","INTERSECT",EDGE,{"derivedFrom":[makeQuery(id+"F9.opExtrude","SWEPT_FACE",FACE,{"disambiguationData":[OSD([sQuery(id+"F8.wireOp",EDGE,"E72.MirrorC")])]}),makeQuery(id+"F12.opExtrude","SWEPT_FACE",FACE,{"disambiguationData":[OSD([sQuery(id+"F11.wireOp",EDGE,"E80.MirrorCS")])]})]});
            var Q12;
            Q12=makeQuery(id+"F12.boolean.opBoolean","INTERSECT",EDGE,{"derivedFrom":[makeQuery(id+"F1.opExtrude","SWEPT_FACE",FACE,{"disambiguationData":[OSD([sQuery(id+"F0.wireOp",EDGE,"E8.MirrorC")])]}),makeQuery(id+"F12.opExtrude","SWEPT_FACE",FACE,{"disambiguationData":[OSD([sQuery(id+"F11.wireOp",EDGE,"E80.MirrorCS")])]})]});
            var Q13;
            Q13=makeQuery(id+"F12.boolean.opBoolean","INTERSECT",EDGE,{"derivedFrom":[makeQuery(id+"F1.opExtrude","SWEPT_FACE",FACE,{"disambiguationData":[OSD([sQuery(id+"F0.wireOp",EDGE,"E8.MirrorC")])]}),makeQuery(id+"F12.opExtrude","SWEPT_FACE",FACE,{"disambiguationData":[OSD([sQuery(id+"F11.wireOp",EDGE,"E78.MirrorCS")])]})]});
            var Q14;
            Q14=makeQuery(id+"F12.boolean.opBoolean","INTERSECT",EDGE,{"derivedFrom":[makeQuery(id+"F9.opExtrude","SWEPT_FACE",FACE,{"disambiguationData":[OSD([sQuery(id+"F8.wireOp",EDGE,"E72.MirrorC")])]}),makeQuery(id+"F12.opExtrude","SWEPT_FACE",FACE,{"disambiguationData":[OSD([sQuery(id+"F11.wireOp",EDGE,"E78.MirrorCS")])]})]});
            var Q15;
            Q15=makeQuery(id+"F12.boolean.opBoolean","INTERSECT",EDGE,{"derivedFrom":[makeQuery(id+"F9.boolean.opBoolean","MERGE",FACE,{"derivedFrom":[makeQuery(id+"F1.opExtrude","SWEPT_FACE",FACE,{"disambiguationData":[OSD([sQuery(id+"F0.wireOp",EDGE,"E13.MirrorC")])]}),makeQuery(id+"F9.opExtrude","SWEPT_FACE",FACE,{"disambiguationData":[OSD([sQuery(id+"F8.wireOp",EDGE,"E71.MirrorC")])]})]}),makeQuery(id+"F12.opExtrude","SWEPT_FACE",FACE,{"disambiguationData":[OSD([sQuery(id+"F11.wireOp",EDGE,"E78.MirrorCS")])]})]});
            var Q16;
            Q16=makeQuery(id+"F12.boolean.opBoolean","INTERSECT",EDGE,{"derivedFrom":[makeQuery(id+"F9.boolean.opBoolean","MERGE",FACE,{"derivedFrom":[makeQuery(id+"F1.opExtrude","SWEPT_FACE",FACE,{"disambiguationData":[OSD([sQuery(id+"F0.wireOp",EDGE,"E13.MirrorC")])]}),makeQuery(id+"F9.opExtrude","SWEPT_FACE",FACE,{"disambiguationData":[OSD([sQuery(id+"F8.wireOp",EDGE,"E71.MirrorC")])]})]}),makeQuery(id+"F12.opExtrude","SWEPT_FACE",FACE,{"disambiguationData":[OSD([sQuery(id+"F11.wireOp",EDGE,"E80.MirrorCS")])]})]});
            var Q17;
            Q17=makeQuery(id+"F12.boolean.opBoolean","INTERSECT",EDGE,{"derivedFrom":[makeQuery(id+"F9.boolean.opBoolean","MERGE",FACE,{"derivedFrom":[makeQuery(id+"F1.opExtrude","SWEPT_FACE",FACE,{"disambiguationData":[OSD([sQuery(id+"F0.wireOp",EDGE,"E12.MirrorC")])]}),makeQuery(id+"F9.opExtrude","SWEPT_FACE",FACE,{"disambiguationData":[OSD([sQuery(id+"F8.wireOp",EDGE,"E69.MirrorC")])]})]}),makeQuery(id+"F12.opExtrude","SWEPT_FACE",FACE,{"disambiguationData":[OSD([sQuery(id+"F11.wireOp",EDGE,"E76")])]})]});
            var Q18;
            Q18=makeQuery(id+"F12.boolean.opBoolean","INTERSECT",EDGE,{"derivedFrom":[makeQuery(id+"F9.opExtrude","SWEPT_FACE",FACE,{"disambiguationData":[OSD([sQuery(id+"F8.wireOp",EDGE,"E70.MirrorC")])]}),makeQuery(id+"F12.opExtrude","SWEPT_FACE",FACE,{"disambiguationData":[OSD([sQuery(id+"F11.wireOp",EDGE,"E76")])]})]});
            var Q19;
            Q19=makeQuery(id+"F12.boolean.opBoolean","INTERSECT",EDGE,{"derivedFrom":[makeQuery(id+"F1.opExtrude","SWEPT_FACE",FACE,{"disambiguationData":[OSD([sQuery(id+"F0.wireOp",EDGE,"E9.MirrorC")])]}),makeQuery(id+"F12.opExtrude","SWEPT_FACE",FACE,{"disambiguationData":[OSD([sQuery(id+"F11.wireOp",EDGE,"E76")])]})]});
            var Q20;
            Q20=makeQuery(id+"F12.boolean.opBoolean","INTERSECT",EDGE,{"derivedFrom":[makeQuery(id+"F9.opExtrude","SWEPT_FACE",FACE,{"disambiguationData":[OSD([sQuery(id+"F8.wireOp",EDGE,"E70.MirrorC")])]}),makeQuery(id+"F12.opExtrude","SWEPT_FACE",FACE,{"disambiguationData":[OSD([sQuery(id+"F11.wireOp",EDGE,"E74")])]})]});
            var Q21;
            Q21=makeQuery(id+"F12.boolean.opBoolean","INTERSECT",EDGE,{"derivedFrom":[makeQuery(id+"F1.opExtrude","SWEPT_FACE",FACE,{"disambiguationData":[OSD([sQuery(id+"F0.wireOp",EDGE,"E9.MirrorC")])]}),makeQuery(id+"F12.opExtrude","SWEPT_FACE",FACE,{"disambiguationData":[OSD([sQuery(id+"F11.wireOp",EDGE,"E74")])]})]});
            var Q22;
            Q22=makeQuery(id+"F12.boolean.opBoolean","INTERSECT",EDGE,{"derivedFrom":[makeQuery(id+"F9.boolean.opBoolean","MERGE",FACE,{"derivedFrom":[makeQuery(id+"F1.opExtrude","SWEPT_FACE",FACE,{"disambiguationData":[OSD([sQuery(id+"F0.wireOp",EDGE,"E12.MirrorC")])]}),makeQuery(id+"F9.opExtrude","SWEPT_FACE",FACE,{"disambiguationData":[OSD([sQuery(id+"F8.wireOp",EDGE,"E69.MirrorC")])]})]}),makeQuery(id+"F12.opExtrude","SWEPT_FACE",FACE,{"disambiguationData":[OSD([sQuery(id+"F11.wireOp",EDGE,"E74")])]})]});
            fillet(context, id + "F13", {"entities" : qUnion([Q0, Q1, Q2, Q3, Q4, Q5, Q6, Q7, Q8, Q9, Q10, Q11, Q12, Q13, Q14, Q15, Q16, Q17, Q18, Q19, Q20, Q21, Q22]), "radius" : 0.62 * mm, "tangentPropagation" : true, "allowEdgeOverflow" : false});
        }
        {
            var Q0;
            {var subQ3=sQuery(id+"F0.wireOp",EDGE,"E28.right");var subQ5=sQuery(id+"F0.wireOp",EDGE,"E38.MirrorCS");var subQ7=sQuery(id+"F0.wireOp",EDGE,"E36.MirrorCS");var subQ9=sQuery(id+"F0.wireOp",EDGE,"E35.MirrorCS");var subQ11=sQuery(id+"F0.wireOp",EDGE,"E34.right");var subQ14=sQuery(id+"F0.wireOp",EDGE,"E29.bottom");var subQ16=sQuery(id+"F0.wireOp",EDGE,"E34.left");var subQ21=sQuery(id+"F0.wireOp",EDGE,"E28.left");var subQ23=sQuery(id+"F0.wireOp",EDGE,"E34.bottom");var subQ26=sQuery(id+"F0.wireOp",EDGE,"E28.top");var subQ28=sQuery(id+"F0.wireOp",EDGE,"E33.MirrorC");var subQ30=sQuery(id+"F0.wireOp",EDGE,"E37.MirrorCS");var subQ31=sQuery(id+"F0.wireOp",EDGE,"E32.MirrorC");var subQ33=sQuery(id+"F0.wireOp",EDGE,"E34.top");var subQ34=sQuery(id+"F0.wireOp",EDGE,"E31.MirrorC");var subQ36=sQuery(id+"F0.wireOp",EDGE,"E30");var subQ39=sQuery(id+"F0.wireOp",EDGE,"E24.MirrorCS");var subQ41=sQuery(id+"F0.wireOp",EDGE,"E29.right");var subQ44=sQuery(id+"F0.wireOp",EDGE,"E23.MirrorCS");var subQ46=sQuery(id+"F0.wireOp",EDGE,"E29.left");var subQ48=sQuery(id+"F0.wireOp",EDGE,"E19");var subQ50=sQuery(id+"F0.wireOp",EDGE,"E18");var subQ52=sQuery(id+"F0.wireOp",EDGE,"E17.right");var subQ54=sQuery(id+"F0.wireOp",EDGE,"E10");var subQ55=makeQuery(id+"F1.opExtrude","SWEPT_FACE",FACE,{"disambiguationData":[OSD([subQ54])]});var subQ56=sQuery(id+"F0.wireOp",EDGE,"E26.MirrorCS");var subQ58=sQuery(id+"F0.wireOp",EDGE,"E17.bottom");var subQ60=sQuery(id+"F0.wireOp",EDGE,"E11.MirrorC");var subQ62=sQuery(id+"F0.wireOp",EDGE,"E28.bottom");var subQ64=sQuery(id+"F0.wireOp",EDGE,"E17.top");var subQ66=sQuery(id+"F0.wireOp",EDGE,"E12.MirrorC");var subQ68=sQuery(id+"F0.wireOp",EDGE,"E17.left");var subQ70=sQuery(id+"F0.wireOp",EDGE,"E13.MirrorC");var subQ72=sQuery(id+"F0.wireOp",EDGE,"E21.MirrorCS");var subQ75=sQuery(id+"F0.wireOp",EDGE,"E22.MirrorCS");var subQ78=sQuery(id+"F0.wireOp",EDGE,"E25.MirrorCS");var subQ80=sQuery(id+"F0.wireOp",EDGE,"E29.top");var subQ82=sQuery(id+"F0.wireOp",EDGE,"E6");var subQ83=sQuery(id+"F0.wireOp",EDGE,"E9.MirrorC");var subQ84=sQuery(id+"F0.wireOp",EDGE,"E7.MirrorC");var subQ85=sQuery(id+"F0.wireOp",EDGE,"E8.MirrorC");Q0=makeQuery(id+"F9.boolean.opBoolean","SPLIT",FACE,{"disambiguationData":[TD([subQ55])],"derivedFrom":makeQuery(id+"F3.boolean.opBoolean","SPLIT",FACE,{"disambiguationData":[TD([makeQuery(id+"F1.opExtrude","SWEPT_FACE",FACE,{"disambiguationData":[OSD([subQ82])]})])],"derivedFrom":makeQuery(id+"F1.opExtrude","CAP_FACE",FACE,{"disambiguationData":[OSD([subQ82,subQ84,subQ85,subQ83,subQ54,subQ60,subQ66,subQ70,sQuery(id+"F0.wireOp",EDGE,"E14.bottom"),sQuery(id+"F0.wireOp",EDGE,"E14.top"),sQuery(id+"F0.wireOp",EDGE,"E14.left"),sQuery(id+"F0.wireOp",EDGE,"E14.right"),sQuery(id+"F0.wireOp",EDGE,"E15.top"),sQuery(id+"F0.wireOp",EDGE,"E15.left"),sQuery(id+"F0.wireOp",EDGE,"E15.right"),sQuery(id+"F0.wireOp",EDGE,"E16.trimOffspring"),subQ58,subQ64,subQ68,subQ52,subQ50,subQ48,subQ72,subQ75,subQ44,subQ39,subQ78,subQ56,subQ62,subQ26,subQ21,subQ3,subQ14,subQ80,subQ46,subQ41,subQ36,subQ34,subQ31,subQ28,subQ23,subQ33,subQ16,subQ11,subQ9,subQ7,subQ30,subQ5,sQuery(id+"F0.wireOp",EDGE,"2JwCXgoE-gSOf-8Eer-RTGS-hlqyIdlCKONg"),sQuery(id+"F0.wireOp",EDGE,"faqvqiBR-mRV4-xvH0-xbDX-PeENiLaSJtV9"),sQuery(id+"F0.wireOp",EDGE,"E39.trimOffspring"),sQuery(id+"F0.wireOp",EDGE,"E40.trimOffspring")])],"isStart":false})})});}
            var sketch = newSketch(context, id + "F14", { "sketchPlane" : qUnion([Q0])});
            skLineSegment(sketch, "E89", {"start": v(-16, 24.5) * mm, "end": v(-19.2, 24.5) * mm});
            skLineSegment(sketch, "E90", {"start": v(-19.2, 24.5) * mm, "end": v(-19.2, 22.1) * mm});
            skLineSegment(sketch, "E91", {"start": v(-19.2, 22.1) * mm, "end": v(-16, 22.1) * mm});
            skLineSegment(sketch, "E92", {"start": v(-16, 4.1) * mm, "end": v(-19.2, 4.1) * mm});
            skLineSegment(sketch, "E93", {"start": v(-19.2, 4.1) * mm, "end": v(-19.2, 1.7) * mm});
            skLineSegment(sketch, "E94", {"start": v(-19.2, 1.7) * mm, "end": v(-16, 1.7) * mm});
            skLineSegment(sketch, "E95", {"start": v(-16, -10.3) * mm, "end": v(-19.2, -10.3) * mm});
            skLineSegment(sketch, "E96", {"start": v(-19.2, -10.3) * mm, "end": v(-19.2, -12.7) * mm});
            skLineSegment(sketch, "E97", {"start": v(-19.2, -12.7) * mm, "end": v(-16, -12.7) * mm});
            skLineSegment(sketch, "E98.MirrorCS", {"start": v(19.2, 4.1) * mm, "end": v(19.2, 1.7) * mm});
            skLineSegment(sketch, "E99.MirrorCS", {"start": v(19.2, 1.7) * mm, "end": v(16, 1.7) * mm});
            skLineSegment(sketch, "E100.MirrorCS", {"start": v(19.2, 22.1) * mm, "end": v(16, 22.1) * mm});
            skLineSegment(sketch, "E101.MirrorCS", {"start": v(16, -10.3) * mm, "end": v(19.2, -10.3) * mm});
            skLineSegment(sketch, "E102.MirrorCS", {"start": v(16, 24.5) * mm, "end": v(19.2, 24.5) * mm});
            skLineSegment(sketch, "E103.MirrorCS", {"start": v(19.2, -10.3) * mm, "end": v(19.2, -12.7) * mm});
            skLineSegment(sketch, "E104.MirrorCS", {"start": v(19.2, -12.7) * mm, "end": v(16, -12.7) * mm});
            skLineSegment(sketch, "E105.MirrorCS", {"start": v(19.2, 24.5) * mm, "end": v(19.2, 22.1) * mm});
            skLineSegment(sketch, "E106.MirrorCS", {"start": v(16, 4.1) * mm, "end": v(19.2, 4.1) * mm});
            skSolve(sketch);
        }
        {
            var Q0;
            {var subQ132=sQuery(id+"F14.wireOp",EDGE,"E89");Q0=makeQuery(id+"F14.imprint","IMPRINT",FACE,{"disambiguationData":[TD([[makeQuery(id+"F14.imprint","IMPRINT",EDGE,{"derivedFrom":subQ132}),1.0]])]});}
            var Q1;
            {var subQ0=sQuery(id+"F14.wireOp",EDGE,"E92");Q1=makeQuery(id+"F14.imprint","IMPRINT",FACE,{"disambiguationData":[TD([[makeQuery(id+"F14.imprint","IMPRINT",EDGE,{"derivedFrom":subQ0}),1.0]])]});}
            var Q2;
            {var subQ0=sQuery(id+"F14.wireOp",EDGE,"E95");Q2=makeQuery(id+"F14.imprint","IMPRINT",FACE,{"disambiguationData":[TD([[makeQuery(id+"F14.imprint","IMPRINT",EDGE,{"derivedFrom":subQ0}),1.0]])]});}
            var Q3;
            {var subQ0=sQuery(id+"F14.wireOp",EDGE,"E101.MirrorCS");Q3=makeQuery(id+"F14.imprint","IMPRINT",FACE,{"disambiguationData":[TD([[makeQuery(id+"F14.imprint","IMPRINT",EDGE,{"derivedFrom":subQ0}),-1.0]])]});}
            var Q4;
            Q4=makeQuery(id+"F14.imprint","IMPRINT",FACE,{"disambiguationData":[TD([[makeQuery(id+"F14.imprint","IMPRINT",EDGE,{"derivedFrom":sQuery(id+"F14.wireOp",EDGE,"E98.MirrorCS")}),-1.0]])]});
            var Q5;
            {var subQ133=sQuery(id+"F14.wireOp",EDGE,"E100.MirrorCS");Q5=makeQuery(id+"F14.imprint","IMPRINT",FACE,{"disambiguationData":[TD([[makeQuery(id+"F14.imprint","IMPRINT",EDGE,{"derivedFrom":subQ133}),-1.0]])]});}
            var Q6;
            {var subQ0=sQuery(id+"F0.wireOp",EDGE,"E14.top");var subQ1=makeQuery(id+"F1.opExtrude","CAP_FACE",FACE,{"disambiguationData":[OSD([sQuery(id+"F0.wireOp",EDGE,"E6"),sQuery(id+"F0.wireOp",EDGE,"E7.MirrorC"),sQuery(id+"F0.wireOp",EDGE,"E8.MirrorC"),sQuery(id+"F0.wireOp",EDGE,"E9.MirrorC"),sQuery(id+"F0.wireOp",EDGE,"E10"),sQuery(id+"F0.wireOp",EDGE,"E11.MirrorC"),sQuery(id+"F0.wireOp",EDGE,"E12.MirrorC"),sQuery(id+"F0.wireOp",EDGE,"E13.MirrorC"),sQuery(id+"F0.wireOp",EDGE,"E14.bottom"),subQ0,sQuery(id+"F0.wireOp",EDGE,"E14.left"),sQuery(id+"F0.wireOp",EDGE,"E14.right"),sQuery(id+"F0.wireOp",EDGE,"E15.top"),sQuery(id+"F0.wireOp",EDGE,"E15.left"),sQuery(id+"F0.wireOp",EDGE,"E15.right"),sQuery(id+"F0.wireOp",EDGE,"E16.trimOffspring"),sQuery(id+"F0.wireOp",EDGE,"E17.bottom"),sQuery(id+"F0.wireOp",EDGE,"E17.top"),sQuery(id+"F0.wireOp",EDGE,"E17.left"),sQuery(id+"F0.wireOp",EDGE,"E17.right"),sQuery(id+"F0.wireOp",EDGE,"E18"),sQuery(id+"F0.wireOp",EDGE,"E19"),sQuery(id+"F0.wireOp",EDGE,"E21.MirrorCS"),sQuery(id+"F0.wireOp",EDGE,"E22.MirrorCS"),sQuery(id+"F0.wireOp",EDGE,"E23.MirrorCS"),sQuery(id+"F0.wireOp",EDGE,"E24.MirrorCS"),sQuery(id+"F0.wireOp",EDGE,"E25.MirrorCS"),sQuery(id+"F0.wireOp",EDGE,"E26.MirrorCS"),sQuery(id+"F0.wireOp",EDGE,"E28.bottom"),sQuery(id+"F0.wireOp",EDGE,"E28.top"),sQuery(id+"F0.wireOp",EDGE,"E28.left"),sQuery(id+"F0.wireOp",EDGE,"E28.right"),sQuery(id+"F0.wireOp",EDGE,"E29.bottom"),sQuery(id+"F0.wireOp",EDGE,"E29.top"),sQuery(id+"F0.wireOp",EDGE,"E29.left"),sQuery(id+"F0.wireOp",EDGE,"E29.right"),sQuery(id+"F0.wireOp",EDGE,"E30"),sQuery(id+"F0.wireOp",EDGE,"E31.MirrorC"),sQuery(id+"F0.wireOp",EDGE,"E32.MirrorC"),sQuery(id+"F0.wireOp",EDGE,"E33.MirrorC"),sQuery(id+"F0.wireOp",EDGE,"E34.bottom"),sQuery(id+"F0.wireOp",EDGE,"E34.top"),sQuery(id+"F0.wireOp",EDGE,"E34.left"),sQuery(id+"F0.wireOp",EDGE,"E34.right"),sQuery(id+"F0.wireOp",EDGE,"E35.MirrorCS"),sQuery(id+"F0.wireOp",EDGE,"E36.MirrorCS"),sQuery(id+"F0.wireOp",EDGE,"E37.MirrorCS"),sQuery(id+"F0.wireOp",EDGE,"E38.MirrorCS"),sQuery(id+"F0.wireOp",EDGE,"2JwCXgoE-gSOf-8Eer-RTGS-hlqyIdlCKONg"),sQuery(id+"F0.wireOp",EDGE,"faqvqiBR-mRV4-xvH0-xbDX-PeENiLaSJtV9"),sQuery(id+"F0.wireOp",EDGE,"E39.trimOffspring"),sQuery(id+"F0.wireOp",EDGE,"E40.trimOffspring")])],"isStart":true});var subQ3=makeQuery(id+"F1.opExtrude","CAP_EDGE",EDGE,{"disambiguationData":[OSD([subQ0])],"isStart":true});Q6=makeQuery(id+"F7.boolean.opBoolean","MERGE",FACE,{"derivedFrom":[subQ1,makeQuery(id+"F7.opExtrude","SWEPT_FACE",FACE,{"disambiguationData":[OSD([subQ0]),TDD([makeQuery(id+"FuSGAjuN3hY24FW_1.boolean.opBoolean","SPLIT",EDGE,{"disambiguationData":[TD([makeQuery(id+"FuSGAjuN3hY24FW_1.opExtrude","SWEPT_FACE",FACE,{"disambiguationData":[OSD([sQuery(id+"FYQ8BpSlA4rBM08_1.wireOp",EDGE,"MOxF5YxK-4EZ1-Xr4a-WxPD-GJG52SWqdB7U")])]})])],"derivedFrom":subQ3})])]}),makeQuery(id+"F7.opExtrude","SWEPT_FACE",FACE,{"disambiguationData":[OSD([subQ0]),TDD([makeQuery(id+"FuSGAjuN3hY24FW_1.boolean.opBoolean","SPLIT",EDGE,{"disambiguationData":[TD([makeQuery(id+"FuSGAjuN3hY24FW_1.opExtrude","SWEPT_FACE",FACE,{"disambiguationData":[OSD([sQuery(id+"FYQ8BpSlA4rBM08_1.wireOp",EDGE,"8e189bec-98aa-4e8d-a065-43acc68c2a770.MirrorCS")])]})])],"derivedFrom":subQ3})])]})]});}
            extrude(context, id + "F15", {"entities" : qUnion([Q0, Q1, Q2, Q3, Q4, Q5]), "operationType" : NewBodyOperationType.ADD, "endBound" : BoundingType.UP_TO_SURFACE, "oppositeDirection" : true, "depth" : 25 * mm, "endBoundEntityFace" : qUnion([Q6]), "offsetDistance" : 25 * mm});
        }
        {
            var Q0;
            {var subQ0=sQuery(id+"F0.wireOp",EDGE,"E14.top");var subQ1=makeQuery(id+"F1.opExtrude","CAP_FACE",FACE,{"disambiguationData":[OSD([sQuery(id+"F0.wireOp",EDGE,"E6"),sQuery(id+"F0.wireOp",EDGE,"E7.MirrorC"),sQuery(id+"F0.wireOp",EDGE,"E8.MirrorC"),sQuery(id+"F0.wireOp",EDGE,"E9.MirrorC"),sQuery(id+"F0.wireOp",EDGE,"E10"),sQuery(id+"F0.wireOp",EDGE,"E11.MirrorC"),sQuery(id+"F0.wireOp",EDGE,"E12.MirrorC"),sQuery(id+"F0.wireOp",EDGE,"E13.MirrorC"),sQuery(id+"F0.wireOp",EDGE,"E14.bottom"),subQ0,sQuery(id+"F0.wireOp",EDGE,"E14.left"),sQuery(id+"F0.wireOp",EDGE,"E14.right"),sQuery(id+"F0.wireOp",EDGE,"E15.top"),sQuery(id+"F0.wireOp",EDGE,"E15.left"),sQuery(id+"F0.wireOp",EDGE,"E15.right"),sQuery(id+"F0.wireOp",EDGE,"E16.trimOffspring"),sQuery(id+"F0.wireOp",EDGE,"E17.bottom"),sQuery(id+"F0.wireOp",EDGE,"E17.top"),sQuery(id+"F0.wireOp",EDGE,"E17.left"),sQuery(id+"F0.wireOp",EDGE,"E17.right"),sQuery(id+"F0.wireOp",EDGE,"E18"),sQuery(id+"F0.wireOp",EDGE,"E19"),sQuery(id+"F0.wireOp",EDGE,"E21.MirrorCS"),sQuery(id+"F0.wireOp",EDGE,"E22.MirrorCS"),sQuery(id+"F0.wireOp",EDGE,"E23.MirrorCS"),sQuery(id+"F0.wireOp",EDGE,"E24.MirrorCS"),sQuery(id+"F0.wireOp",EDGE,"E25.MirrorCS"),sQuery(id+"F0.wireOp",EDGE,"E26.MirrorCS"),sQuery(id+"F0.wireOp",EDGE,"E28.bottom"),sQuery(id+"F0.wireOp",EDGE,"E28.top"),sQuery(id+"F0.wireOp",EDGE,"E28.left"),sQuery(id+"F0.wireOp",EDGE,"E28.right"),sQuery(id+"F0.wireOp",EDGE,"E29.bottom"),sQuery(id+"F0.wireOp",EDGE,"E29.top"),sQuery(id+"F0.wireOp",EDGE,"E29.left"),sQuery(id+"F0.wireOp",EDGE,"E29.right"),sQuery(id+"F0.wireOp",EDGE,"E30"),sQuery(id+"F0.wireOp",EDGE,"E31.MirrorC"),sQuery(id+"F0.wireOp",EDGE,"E32.MirrorC"),sQuery(id+"F0.wireOp",EDGE,"E33.MirrorC"),sQuery(id+"F0.wireOp",EDGE,"E34.bottom"),sQuery(id+"F0.wireOp",EDGE,"E34.top"),sQuery(id+"F0.wireOp",EDGE,"E34.left"),sQuery(id+"F0.wireOp",EDGE,"E34.right"),sQuery(id+"F0.wireOp",EDGE,"E35.MirrorCS"),sQuery(id+"F0.wireOp",EDGE,"E36.MirrorCS"),sQuery(id+"F0.wireOp",EDGE,"E37.MirrorCS"),sQuery(id+"F0.wireOp",EDGE,"E38.MirrorCS"),sQuery(id+"F0.wireOp",EDGE,"2JwCXgoE-gSOf-8Eer-RTGS-hlqyIdlCKONg"),sQuery(id+"F0.wireOp",EDGE,"faqvqiBR-mRV4-xvH0-xbDX-PeENiLaSJtV9"),sQuery(id+"F0.wireOp",EDGE,"E39.trimOffspring"),sQuery(id+"F0.wireOp",EDGE,"E40.trimOffspring")])],"isStart":true});var subQ3=makeQuery(id+"F1.opExtrude","CAP_EDGE",EDGE,{"disambiguationData":[OSD([subQ0])],"isStart":true});Q0=makeQuery(id+"F7.boolean.opBoolean","MERGE",FACE,{"derivedFrom":[subQ1,makeQuery(id+"F7.opExtrude","SWEPT_FACE",FACE,{"disambiguationData":[OSD([subQ0]),TDD([makeQuery(id+"FuSGAjuN3hY24FW_1.boolean.opBoolean","SPLIT",EDGE,{"disambiguationData":[TD([makeQuery(id+"FuSGAjuN3hY24FW_1.opExtrude","SWEPT_FACE",FACE,{"disambiguationData":[OSD([sQuery(id+"FYQ8BpSlA4rBM08_1.wireOp",EDGE,"MOxF5YxK-4EZ1-Xr4a-WxPD-GJG52SWqdB7U")])]})])],"derivedFrom":subQ3})])]}),makeQuery(id+"F7.opExtrude","SWEPT_FACE",FACE,{"disambiguationData":[OSD([subQ0]),TDD([makeQuery(id+"FuSGAjuN3hY24FW_1.boolean.opBoolean","SPLIT",EDGE,{"disambiguationData":[TD([makeQuery(id+"FuSGAjuN3hY24FW_1.opExtrude","SWEPT_FACE",FACE,{"disambiguationData":[OSD([sQuery(id+"FYQ8BpSlA4rBM08_1.wireOp",EDGE,"8e189bec-98aa-4e8d-a065-43acc68c2a770.MirrorCS")])]})])],"derivedFrom":subQ3})])]})]});}
            var sketch = newSketch(context, id + "F16", { "sketchPlane" : qUnion([Q0])});
            skCircle(sketch, "E107", {"center": v(37, -37.5) * mm, "radius": 8 * mm});
            skCircle(sketch, "E108", {"center": v(37, -37.5) * mm, "radius": 3.65 * mm});
            skCircle(sketch, "E109.MirrorC", {"center": v(-37, -37.5) * mm, "radius": 8 * mm});
            skCircle(sketch, "E110.MirrorC", {"center": v(-37, -37.5) * mm, "radius": 3.65 * mm});
            skCircle(sketch, "E111.MirrorC", {"center": v(37, 37.5) * mm, "radius": 8 * mm});
            skCircle(sketch, "E112.MirrorC", {"center": v(-37, 37.5) * mm, "radius": 8 * mm});
            skCircle(sketch, "E113.MirrorC", {"center": v(37, 37.5) * mm, "radius": 3.65 * mm});
            skCircle(sketch, "E114.MirrorC", {"center": v(-37, 37.5) * mm, "radius": 3.65 * mm});
            skSolve(sketch);
        }
        {
            var Q0;
            Q0 = qSketchRegion(id + "F16", true);
            extrude(context, id + "F17", {"entities" : qUnion([Q0]), "operationType" : NewBodyOperationType.ADD, "oppositeDirection" : true, "depth" : 0.3 * mm, "offsetDistance" : 25 * mm});
        }
        {
            var Q0;
            {var subQ0=sQuery(id+"F0.wireOp",EDGE,"E17.right");var subQ1=sQuery(id+"F5.wireOp",EDGE,"12a840b2-8adb-4d60-9d90-1feae7f4b4324.MirrorCS");var subQ2=sQuery(id+"F5.wireOp",EDGE,"12a840b2-8adb-4d60-9d90-1feae7f4b4323.MirrorCS");var subQ3=sQuery(id+"F5.wireOp",EDGE,"12a840b2-8adb-4d60-9d90-1feae7f4b4321.MirrorCS");var subQ4=sQuery(id+"F5.wireOp",EDGE,"12a840b2-8adb-4d60-9d90-1feae7f4b4320.MirrorCS");var subQ5=sQuery(id+"F5.wireOp",EDGE,"TwUVh8Jm-KBbL-sydY-1FMm-F6mmMaZqGzpT.right");var subQ6=sQuery(id+"F5.wireOp",EDGE,"TwUVh8Jm-KBbL-sydY-1FMm-F6mmMaZqGzpT.left");var subQ7=sQuery(id+"F5.wireOp",EDGE,"TwUVh8Jm-KBbL-sydY-1FMm-F6mmMaZqGzpT.top");var subQ8=sQuery(id+"F5.wireOp",EDGE,"TwUVh8Jm-KBbL-sydY-1FMm-F6mmMaZqGzpT.bottom");var subQ9=sQuery(id+"F5.wireOp",EDGE,"E58.right");var subQ10=sQuery(id+"F5.wireOp",EDGE,"E58.left");var subQ11=sQuery(id+"F5.wireOp",EDGE,"E58.top");var subQ12=sQuery(id+"F5.wireOp",EDGE,"E58.bottom");var subQ13=sQuery(id+"F0.wireOp",EDGE,"E40.trimOffspring");var subQ14=sQuery(id+"F0.wireOp",EDGE,"E39.trimOffspring");var subQ15=sQuery(id+"F0.wireOp",EDGE,"faqvqiBR-mRV4-xvH0-xbDX-PeENiLaSJtV9");var subQ16=sQuery(id+"F0.wireOp",EDGE,"2JwCXgoE-gSOf-8Eer-RTGS-hlqyIdlCKONg");var subQ17=sQuery(id+"F0.wireOp",EDGE,"E38.MirrorCS");var subQ18=sQuery(id+"F0.wireOp",EDGE,"E37.MirrorCS");var subQ19=sQuery(id+"F0.wireOp",EDGE,"E36.MirrorCS");var subQ20=sQuery(id+"F0.wireOp",EDGE,"E35.MirrorCS");var subQ21=sQuery(id+"F0.wireOp",EDGE,"E34.right");var subQ22=sQuery(id+"F0.wireOp",EDGE,"E34.left");var subQ23=sQuery(id+"F0.wireOp",EDGE,"E34.top");var subQ24=sQuery(id+"F0.wireOp",EDGE,"E34.bottom");var subQ25=sQuery(id+"F0.wireOp",EDGE,"E33.MirrorC");var subQ26=sQuery(id+"F0.wireOp",EDGE,"E32.MirrorC");var subQ27=sQuery(id+"F0.wireOp",EDGE,"E31.MirrorC");var subQ28=sQuery(id+"F0.wireOp",EDGE,"E30");var subQ29=sQuery(id+"F0.wireOp",EDGE,"E29.right");var subQ30=sQuery(id+"F0.wireOp",EDGE,"E29.left");var subQ31=sQuery(id+"F0.wireOp",EDGE,"E29.top");var subQ32=sQuery(id+"F0.wireOp",EDGE,"E29.bottom");var subQ33=sQuery(id+"F0.wireOp",EDGE,"E28.right");var subQ34=sQuery(id+"F0.wireOp",EDGE,"E28.left");var subQ35=sQuery(id+"F0.wireOp",EDGE,"E28.top");var subQ36=sQuery(id+"F0.wireOp",EDGE,"E28.bottom");var subQ37=sQuery(id+"F0.wireOp",EDGE,"E26.MirrorCS");var subQ38=sQuery(id+"F0.wireOp",EDGE,"E25.MirrorCS");var subQ39=sQuery(id+"F0.wireOp",EDGE,"E24.MirrorCS");var subQ40=sQuery(id+"F0.wireOp",EDGE,"E23.MirrorCS");var subQ41=sQuery(id+"F0.wireOp",EDGE,"E22.MirrorCS");var subQ42=sQuery(id+"F0.wireOp",EDGE,"E21.MirrorCS");var subQ43=sQuery(id+"F0.wireOp",EDGE,"E19");var subQ44=sQuery(id+"F0.wireOp",EDGE,"E18");var subQ45=sQuery(id+"F0.wireOp",EDGE,"E17.left");var subQ46=sQuery(id+"F0.wireOp",EDGE,"E17.top");var subQ47=sQuery(id+"F0.wireOp",EDGE,"E17.bottom");var subQ48=sQuery(id+"F0.wireOp",EDGE,"E16.trimOffspring");var subQ49=sQuery(id+"F0.wireOp",EDGE,"E15.right");var subQ50=sQuery(id+"F0.wireOp",EDGE,"E15.left");var subQ51=sQuery(id+"F0.wireOp",EDGE,"E15.top");var subQ52=sQuery(id+"F0.wireOp",EDGE,"E14.right");var subQ53=sQuery(id+"F0.wireOp",EDGE,"E14.left");var subQ54=sQuery(id+"F0.wireOp",EDGE,"E14.top");var subQ55=sQuery(id+"F0.wireOp",EDGE,"E14.bottom");var subQ56=sQuery(id+"F0.wireOp",EDGE,"E13.MirrorC");var subQ57=sQuery(id+"F0.wireOp",EDGE,"E12.MirrorC");var subQ58=sQuery(id+"F0.wireOp",EDGE,"E11.MirrorC");var subQ59=sQuery(id+"F0.wireOp",EDGE,"E10");var subQ60=sQuery(id+"F0.wireOp",EDGE,"E9.MirrorC");var subQ61=sQuery(id+"F0.wireOp",EDGE,"E8.MirrorC");var subQ62=sQuery(id+"F0.wireOp",EDGE,"E7.MirrorC");var subQ63=sQuery(id+"F0.wireOp",EDGE,"E6");var subQ101=makeQuery(id+"F1.opExtrude","SWEPT_FACE",FACE,{"disambiguationData":[OSD([subQ55])]});var subQ103=makeQuery(id+"F1.opExtrude","SWEPT_FACE",FACE,{"disambiguationData":[OSD([subQ59])]});var subQ125=makeQuery(id+"F1.opExtrude","CAP_FACE",FACE,{"disambiguationData":[OSD([subQ63,subQ62,subQ61,subQ60,subQ59,subQ58,subQ57,subQ56,subQ55,subQ54,subQ53,subQ52,subQ51,subQ50,subQ49,subQ48,subQ47,subQ46,subQ45,subQ0,subQ44,subQ43,subQ42,subQ41,subQ40,subQ39,subQ38,subQ37,subQ36,subQ35,subQ34,subQ33,subQ32,subQ31,subQ30,subQ29,subQ28,subQ27,subQ26,subQ25,subQ24,subQ23,subQ22,subQ21,subQ20,subQ19,subQ18,subQ17,subQ16,subQ15,subQ14,subQ13])],"isStart":false});Q0=makeQuery(id+"F15.boolean.opBoolean","MERGE",FACE,{"derivedFrom":[makeQuery(id+"F9.boolean.opBoolean","SPLIT",FACE,{"disambiguationData":[TD([subQ103])],"derivedFrom":makeQuery(id+"F6.boolean.opBoolean","MERGE",FACE,{"derivedFrom":[makeQuery(id+"FuSGAjuN3hY24FW_1.boolean.opBoolean","SPLIT",FACE,{"disambiguationData":[TD([subQ101])],"derivedFrom":makeQuery(id+"F3.boolean.opBoolean","SPLIT",FACE,{"disambiguationData":[TD([subQ101])],"derivedFrom":subQ125})}),makeQuery(id+"F3.boolean.opBoolean","SPLIT",FACE,{"disambiguationData":[TD([makeQuery(id+"F1.opExtrude","SWEPT_FACE",FACE,{"disambiguationData":[OSD([subQ63])]})])],"derivedFrom":subQ125})],"fromTools":[makeQuery(id+"F6.opExtrude","CAP_FACE",FACE,{"disambiguationData":[OSD([subQ12,subQ11,subQ10,subQ9])],"isStart":false}),makeQuery(id+"F6.opExtrude","CAP_FACE",FACE,{"disambiguationData":[OSD([subQ8,subQ7,subQ6,subQ5])],"isStart":false}),makeQuery(id+"F6.opExtrude","CAP_FACE",FACE,{"disambiguationData":[OSD([subQ4,subQ3,subQ2,subQ1])],"isStart":false})]})}),makeQuery(id+"F15.opExtrude","CAP_FACE",FACE,{"disambiguationData":[OSD([subQ63,subQ62,subQ61,subQ60,subQ59,subQ58,subQ57,subQ56,subQ55,subQ54,subQ53,subQ52,subQ51,subQ50,subQ49,subQ48,subQ47,subQ46,subQ45,subQ0,subQ44,subQ43,subQ42,subQ41,subQ40,subQ39,subQ38,subQ37,subQ36,subQ35,subQ34,subQ33,subQ32,subQ31,subQ30,subQ29,subQ28,subQ27,subQ26,subQ25,subQ24,subQ23,subQ22,subQ21,subQ20,subQ19,subQ18,subQ17,subQ16,subQ15,subQ14,subQ13,subQ12,subQ11,subQ10,subQ9,subQ8,subQ7,subQ6,subQ5,subQ4,subQ3,subQ2,subQ1,sQuery(id+"F14.wireOp",EDGE,"E89"),sQuery(id+"F14.wireOp",EDGE,"E90"),sQuery(id+"F14.wireOp",EDGE,"E91")])],"isStart":true}),makeQuery(id+"F15.opExtrude","CAP_FACE",FACE,{"disambiguationData":[OSD([subQ45,sQuery(id+"F14.wireOp",EDGE,"E92"),sQuery(id+"F14.wireOp",EDGE,"E93"),sQuery(id+"F14.wireOp",EDGE,"E94")])],"isStart":true}),makeQuery(id+"F15.opExtrude","CAP_FACE",FACE,{"disambiguationData":[OSD([subQ45,sQuery(id+"F14.wireOp",EDGE,"E95"),sQuery(id+"F14.wireOp",EDGE,"E96"),sQuery(id+"F14.wireOp",EDGE,"E97")])],"isStart":true}),makeQuery(id+"F15.opExtrude","CAP_FACE",FACE,{"disambiguationData":[OSD([subQ0,sQuery(id+"F14.wireOp",EDGE,"E98.MirrorCS"),sQuery(id+"F14.wireOp",EDGE,"E99.MirrorCS"),sQuery(id+"F14.wireOp",EDGE,"E106.MirrorCS")])],"isStart":true}),makeQuery(id+"F15.opExtrude","CAP_FACE",FACE,{"disambiguationData":[OSD([subQ63,subQ62,subQ61,subQ60,subQ59,subQ58,subQ57,subQ56,subQ55,subQ54,subQ53,subQ52,subQ51,subQ50,subQ49,subQ48,subQ47,subQ46,subQ45,subQ0,subQ44,subQ43,subQ42,subQ41,subQ40,subQ39,subQ38,subQ37,subQ36,subQ35,subQ34,subQ33,subQ32,subQ31,subQ30,subQ29,subQ28,subQ27,subQ26,subQ25,subQ24,subQ23,subQ22,subQ21,subQ20,subQ19,subQ18,subQ17,subQ16,subQ15,subQ14,subQ13,subQ12,subQ11,subQ10,subQ9,subQ8,subQ7,subQ6,subQ5,subQ4,subQ3,subQ2,subQ1,sQuery(id+"F14.wireOp",EDGE,"E100.MirrorCS"),sQuery(id+"F14.wireOp",EDGE,"E102.MirrorCS"),sQuery(id+"F14.wireOp",EDGE,"E105.MirrorCS")])],"isStart":true}),makeQuery(id+"F15.opExtrude","CAP_FACE",FACE,{"disambiguationData":[OSD([subQ0,sQuery(id+"F14.wireOp",EDGE,"E101.MirrorCS"),sQuery(id+"F14.wireOp",EDGE,"E103.MirrorCS"),sQuery(id+"F14.wireOp",EDGE,"E104.MirrorCS")])],"isStart":true})]});}
            var sketch = newSketch(context, id + "F18", { "sketchPlane" : qUnion([Q0])});
            skLineSegment(sketch, "E115.0", {"start": v(-30.59, -38.57) * mm, "end": v(-16.8, -34.72) * mm});
            skLineSegment(sketch, "E116.0", {"start": v(-15.18, -34.5) * mm, "end": v(15.18, -34.5) * mm});
            skLineSegment(sketch, "E117.0", {"start": v(30.59, -38.57) * mm, "end": v(16.8, -34.72) * mm});
            skArc(sketch, "E118.0", {"start": v(15.18, -34.5) * mm, "mid": v(16, -34.56) * mm, "end": v(16.8, -34.72) * mm});
            skArc(sketch, "E119.0", {"start": v(-16.8, -34.72) * mm, "mid": v(-16, -34.56) * mm, "end": v(-15.18, -34.5) * mm});
            skLineSegment(sketch, "E120", {"start": v(-30.53, -36.89) * mm, "end": v(-16.88, -33.08) * mm});
            skLineSegment(sketch, "E121", {"start": v(-15.53, -32.9) * mm, "end": v(15.53, -32.9) * mm});
            skLineSegment(sketch, "E122", {"start": v(16.88, -33.08) * mm, "end": v(30.53, -36.89) * mm});
            skPoint(sketch, "E123.visualSharp", {"position": v(-16.22, -32.9) * mm});
            skArc(sketch, "E123.filletArc", {"start": v(-15.53, -32.9) * mm, "mid": v(-16.21, -32.95) * mm, "end": v(-16.88, -33.08) * mm});
            skPoint(sketch, "E124.visualSharp", {"position": v(16.22, -32.9) * mm});
            skArc(sketch, "E124.filletArc", {"start": v(16.88, -33.08) * mm, "mid": v(16.21, -32.95) * mm, "end": v(15.53, -32.9) * mm});
            skLineSegment(sketch, "E125", {"start": v(-30.59, 38.57) * mm, "end": v(-8.85, 32.5) * mm});
            skLineSegment(sketch, "E126", {"start": v(-8.85, 32.5) * mm, "end": v(-8.85, 30.85) * mm});
            skLineSegment(sketch, "E127", {"start": v(-8.85, 30.85) * mm, "end": v(-30.53, 36.89) * mm});
            skLineSegment(sketch, "E128.MirrorCS", {"start": v(8.85, 30.85) * mm, "end": v(30.53, 36.89) * mm});
            skLineSegment(sketch, "E129.MirrorCS", {"start": v(8.85, 32.5) * mm, "end": v(8.85, 30.85) * mm});
            skLineSegment(sketch, "E130.MirrorCS", {"start": v(30.59, 38.57) * mm, "end": v(8.85, 32.5) * mm});
            skSolve(sketch);
        }
        {
            var Q0;
            {var subQ1=sQuery(id+"F18.wireOp",EDGE,"E126");Q0=makeQuery(id+"F18.imprint","IMPRINT",FACE,{"disambiguationData":[TD([[makeQuery(id+"F18.imprint","IMPRINT",EDGE,{"derivedFrom":subQ1}),1.0]])]});}
            var Q1;
            {var subQ135=sQuery(id+"F18.wireOp",EDGE,"E128.MirrorCS");Q1=makeQuery(id+"F18.imprint","IMPRINT",FACE,{"disambiguationData":[TD([[makeQuery(id+"F18.imprint","IMPRINT",EDGE,{"derivedFrom":subQ135}),1.0]])]});}
            var Q2;
            {var subQ0=sQuery(id+"F18.wireOp",EDGE,"E115.0");Q2=makeQuery(id+"F18.imprint","IMPRINT",FACE,{"disambiguationData":[TD([[makeQuery(id+"F18.imprint","IMPRINT",EDGE,{"derivedFrom":subQ0}),1.0]])]});}
            extrude(context, id + "F19", {"entities" : qUnion([Q0, Q1, Q2]), "operationType" : NewBodyOperationType.ADD, "depth" : 0.8 * mm, "offsetDistance" : 25 * mm});
        }
        {
            var Q0;
            {var subQ0=sQuery(id+"F0.wireOp",EDGE,"E9.MirrorC");var subQ1=makeQuery(id+"F1.opExtrude","SWEPT_FACE",FACE,{"disambiguationData":[OSD([subQ0])]});var subQ2=sQuery(id+"F0.wireOp",EDGE,"E38.MirrorCS");var subQ3=sQuery(id+"F0.wireOp",EDGE,"E37.MirrorCS");var subQ4=sQuery(id+"F0.wireOp",EDGE,"E35.MirrorCS");var subQ5=sQuery(id+"F0.wireOp",EDGE,"E34.right");var subQ6=sQuery(id+"F0.wireOp",EDGE,"E34.left");var subQ7=sQuery(id+"F0.wireOp",EDGE,"E34.top");var subQ8=sQuery(id+"F0.wireOp",EDGE,"E28.left");var subQ9=sQuery(id+"F0.wireOp",EDGE,"E34.bottom");var subQ10=sQuery(id+"F0.wireOp",EDGE,"E28.top");var subQ11=sQuery(id+"F0.wireOp",EDGE,"E33.MirrorC");var subQ12=sQuery(id+"F0.wireOp",EDGE,"E32.MirrorC");var subQ13=sQuery(id+"F0.wireOp",EDGE,"E31.MirrorC");var subQ14=sQuery(id+"F0.wireOp",EDGE,"E30");var subQ15=sQuery(id+"F0.wireOp",EDGE,"E24.MirrorCS");var subQ16=sQuery(id+"F0.wireOp",EDGE,"E29.right");var subQ17=sQuery(id+"F0.wireOp",EDGE,"E23.MirrorCS");var subQ18=sQuery(id+"F0.wireOp",EDGE,"E29.left");var subQ19=sQuery(id+"F0.wireOp",EDGE,"E22.MirrorCS");var subQ20=sQuery(id+"F0.wireOp",EDGE,"E29.top");var subQ21=sQuery(id+"F0.wireOp",EDGE,"E21.MirrorCS");var subQ22=sQuery(id+"F0.wireOp",EDGE,"E29.bottom");var subQ23=sQuery(id+"F0.wireOp",EDGE,"E28.right");var subQ24=sQuery(id+"F0.wireOp",EDGE,"E13.MirrorC");var subQ25=sQuery(id+"F0.wireOp",EDGE,"E17.top");var subQ26=sQuery(id+"F0.wireOp",EDGE,"E12.MirrorC");var subQ27=sQuery(id+"F0.wireOp",EDGE,"E17.bottom");var subQ28=sQuery(id+"F0.wireOp",EDGE,"E11.MirrorC");var subQ29=sQuery(id+"F0.wireOp",EDGE,"E28.bottom");var subQ30=sQuery(id+"F0.wireOp",EDGE,"E10");var subQ31=sQuery(id+"F0.wireOp",EDGE,"E26.MirrorCS");var subQ32=sQuery(id+"F0.wireOp",EDGE,"E36.MirrorCS");var subQ33=sQuery(id+"F0.wireOp",EDGE,"E6");var subQ34=sQuery(id+"F0.wireOp",EDGE,"E19");var subQ35=sQuery(id+"F0.wireOp",EDGE,"E25.MirrorCS");var subQ36=sQuery(id+"F0.wireOp",EDGE,"E7.MirrorC");var subQ37=sQuery(id+"F0.wireOp",EDGE,"E8.MirrorC");var subQ38=sQuery(id+"F0.wireOp",EDGE,"E17.left");var subQ39=sQuery(id+"F0.wireOp",EDGE,"E17.right");var subQ40=sQuery(id+"F0.wireOp",EDGE,"E18");var subQ41=sQuery(id+"F0.wireOp",EDGE,"E40.trimOffspring");var subQ42=sQuery(id+"F0.wireOp",EDGE,"E39.trimOffspring");var subQ43=sQuery(id+"F0.wireOp",EDGE,"faqvqiBR-mRV4-xvH0-xbDX-PeENiLaSJtV9");var subQ44=sQuery(id+"F0.wireOp",EDGE,"2JwCXgoE-gSOf-8Eer-RTGS-hlqyIdlCKONg");var subQ45=sQuery(id+"F0.wireOp",EDGE,"E16.trimOffspring");var subQ46=sQuery(id+"F0.wireOp",EDGE,"E15.right");var subQ47=sQuery(id+"F0.wireOp",EDGE,"E15.left");var subQ48=sQuery(id+"F0.wireOp",EDGE,"E15.top");var subQ49=sQuery(id+"F0.wireOp",EDGE,"E14.right");var subQ50=sQuery(id+"F0.wireOp",EDGE,"E14.left");var subQ51=sQuery(id+"F0.wireOp",EDGE,"E14.top");var subQ52=sQuery(id+"F0.wireOp",EDGE,"E14.bottom");var subQ53=makeQuery(id+"F1.opExtrude","CAP_FACE",FACE,{"disambiguationData":[OSD([subQ33,subQ36,subQ37,subQ0,subQ30,subQ28,subQ26,subQ24,subQ52,subQ51,subQ50,subQ49,subQ48,subQ47,subQ46,subQ45,subQ27,subQ25,subQ38,subQ39,subQ40,subQ34,subQ21,subQ19,subQ17,subQ15,subQ35,subQ31,subQ29,subQ10,subQ8,subQ23,subQ22,subQ20,subQ18,subQ16,subQ14,subQ13,subQ12,subQ11,subQ9,subQ7,subQ6,subQ5,subQ4,subQ32,subQ3,subQ2,subQ44,subQ43,subQ42,subQ41])],"isStart":false});var subQ63=makeQuery(id+"F1.opExtrude","SWEPT_FACE",FACE,{"disambiguationData":[OSD([subQ52])]});Q0=makeQuery(id+"F9.boolean.opBoolean","SPLIT",FACE,{"disambiguationData":[TD([subQ1])],"derivedFrom":makeQuery(id+"F6.boolean.opBoolean","MERGE",FACE,{"derivedFrom":[makeQuery(id+"FuSGAjuN3hY24FW_1.boolean.opBoolean","SPLIT",FACE,{"disambiguationData":[TD([subQ63])],"derivedFrom":makeQuery(id+"F3.boolean.opBoolean","SPLIT",FACE,{"disambiguationData":[TD([subQ63])],"derivedFrom":subQ53})}),makeQuery(id+"F3.boolean.opBoolean","SPLIT",FACE,{"disambiguationData":[TD([makeQuery(id+"F1.opExtrude","SWEPT_FACE",FACE,{"disambiguationData":[OSD([subQ33])]})])],"derivedFrom":subQ53})],"fromTools":[makeQuery(id+"F6.opExtrude","CAP_FACE",FACE,{"disambiguationData":[OSD([sQuery(id+"F5.wireOp",EDGE,"E58.bottom"),sQuery(id+"F5.wireOp",EDGE,"E58.top"),sQuery(id+"F5.wireOp",EDGE,"E58.left"),sQuery(id+"F5.wireOp",EDGE,"E58.right")])],"isStart":false}),makeQuery(id+"F6.opExtrude","CAP_FACE",FACE,{"disambiguationData":[OSD([sQuery(id+"F5.wireOp",EDGE,"TwUVh8Jm-KBbL-sydY-1FMm-F6mmMaZqGzpT.bottom"),sQuery(id+"F5.wireOp",EDGE,"TwUVh8Jm-KBbL-sydY-1FMm-F6mmMaZqGzpT.top"),sQuery(id+"F5.wireOp",EDGE,"TwUVh8Jm-KBbL-sydY-1FMm-F6mmMaZqGzpT.left"),sQuery(id+"F5.wireOp",EDGE,"TwUVh8Jm-KBbL-sydY-1FMm-F6mmMaZqGzpT.right")])],"isStart":false}),makeQuery(id+"F6.opExtrude","CAP_FACE",FACE,{"disambiguationData":[OSD([sQuery(id+"F5.wireOp",EDGE,"12a840b2-8adb-4d60-9d90-1feae7f4b4320.MirrorCS"),sQuery(id+"F5.wireOp",EDGE,"12a840b2-8adb-4d60-9d90-1feae7f4b4321.MirrorCS"),sQuery(id+"F5.wireOp",EDGE,"12a840b2-8adb-4d60-9d90-1feae7f4b4323.MirrorCS"),sQuery(id+"F5.wireOp",EDGE,"12a840b2-8adb-4d60-9d90-1feae7f4b4324.MirrorCS")])],"isStart":false})]})});}
            var Q1;
            {var subQ0=sQuery(id+"F0.wireOp",EDGE,"E6");var subQ1=makeQuery(id+"F1.opExtrude","SWEPT_FACE",FACE,{"disambiguationData":[OSD([subQ0])]});var subQ2=sQuery(id+"F0.wireOp",EDGE,"E38.MirrorCS");var subQ3=sQuery(id+"F0.wireOp",EDGE,"E37.MirrorCS");var subQ4=sQuery(id+"F0.wireOp",EDGE,"E35.MirrorCS");var subQ5=sQuery(id+"F0.wireOp",EDGE,"E34.right");var subQ6=sQuery(id+"F0.wireOp",EDGE,"E34.left");var subQ7=sQuery(id+"F0.wireOp",EDGE,"E34.top");var subQ8=sQuery(id+"F0.wireOp",EDGE,"E28.left");var subQ9=sQuery(id+"F0.wireOp",EDGE,"E34.bottom");var subQ10=sQuery(id+"F0.wireOp",EDGE,"E28.top");var subQ11=sQuery(id+"F0.wireOp",EDGE,"E33.MirrorC");var subQ12=sQuery(id+"F0.wireOp",EDGE,"E32.MirrorC");var subQ13=sQuery(id+"F0.wireOp",EDGE,"E31.MirrorC");var subQ14=sQuery(id+"F0.wireOp",EDGE,"E30");var subQ15=sQuery(id+"F0.wireOp",EDGE,"E24.MirrorCS");var subQ16=sQuery(id+"F0.wireOp",EDGE,"E29.right");var subQ17=sQuery(id+"F0.wireOp",EDGE,"E23.MirrorCS");var subQ18=sQuery(id+"F0.wireOp",EDGE,"E29.left");var subQ19=sQuery(id+"F0.wireOp",EDGE,"E22.MirrorCS");var subQ20=sQuery(id+"F0.wireOp",EDGE,"E29.top");var subQ21=sQuery(id+"F0.wireOp",EDGE,"E21.MirrorCS");var subQ22=sQuery(id+"F0.wireOp",EDGE,"E29.bottom");var subQ23=sQuery(id+"F0.wireOp",EDGE,"E28.right");var subQ24=sQuery(id+"F0.wireOp",EDGE,"E13.MirrorC");var subQ25=sQuery(id+"F0.wireOp",EDGE,"E17.top");var subQ26=sQuery(id+"F0.wireOp",EDGE,"E12.MirrorC");var subQ27=sQuery(id+"F0.wireOp",EDGE,"E17.bottom");var subQ28=sQuery(id+"F0.wireOp",EDGE,"E11.MirrorC");var subQ29=sQuery(id+"F0.wireOp",EDGE,"E28.bottom");var subQ30=sQuery(id+"F0.wireOp",EDGE,"E10");var subQ31=sQuery(id+"F0.wireOp",EDGE,"E26.MirrorCS");var subQ32=sQuery(id+"F0.wireOp",EDGE,"E36.MirrorCS");var subQ33=sQuery(id+"F0.wireOp",EDGE,"E19");var subQ34=sQuery(id+"F0.wireOp",EDGE,"E9.MirrorC");var subQ35=sQuery(id+"F0.wireOp",EDGE,"E25.MirrorCS");var subQ36=sQuery(id+"F0.wireOp",EDGE,"E7.MirrorC");var subQ37=sQuery(id+"F0.wireOp",EDGE,"E8.MirrorC");var subQ38=sQuery(id+"F0.wireOp",EDGE,"E17.left");var subQ39=sQuery(id+"F0.wireOp",EDGE,"E17.right");var subQ40=sQuery(id+"F0.wireOp",EDGE,"E18");var subQ41=sQuery(id+"F0.wireOp",EDGE,"E40.trimOffspring");var subQ42=sQuery(id+"F0.wireOp",EDGE,"E39.trimOffspring");var subQ43=sQuery(id+"F0.wireOp",EDGE,"faqvqiBR-mRV4-xvH0-xbDX-PeENiLaSJtV9");var subQ44=sQuery(id+"F0.wireOp",EDGE,"2JwCXgoE-gSOf-8Eer-RTGS-hlqyIdlCKONg");var subQ45=sQuery(id+"F0.wireOp",EDGE,"E16.trimOffspring");var subQ46=sQuery(id+"F0.wireOp",EDGE,"E15.right");var subQ47=sQuery(id+"F0.wireOp",EDGE,"E15.left");var subQ48=sQuery(id+"F0.wireOp",EDGE,"E15.top");var subQ49=sQuery(id+"F0.wireOp",EDGE,"E14.right");var subQ50=sQuery(id+"F0.wireOp",EDGE,"E14.left");var subQ51=sQuery(id+"F0.wireOp",EDGE,"E14.top");var subQ52=sQuery(id+"F0.wireOp",EDGE,"E14.bottom");var subQ53=makeQuery(id+"F1.opExtrude","CAP_FACE",FACE,{"disambiguationData":[OSD([subQ0,subQ36,subQ37,subQ34,subQ30,subQ28,subQ26,subQ24,subQ52,subQ51,subQ50,subQ49,subQ48,subQ47,subQ46,subQ45,subQ27,subQ25,subQ38,subQ39,subQ40,subQ33,subQ21,subQ19,subQ17,subQ15,subQ35,subQ31,subQ29,subQ10,subQ8,subQ23,subQ22,subQ20,subQ18,subQ16,subQ14,subQ13,subQ12,subQ11,subQ9,subQ7,subQ6,subQ5,subQ4,subQ32,subQ3,subQ2,subQ44,subQ43,subQ42,subQ41])],"isStart":false});var subQ63=makeQuery(id+"F1.opExtrude","SWEPT_FACE",FACE,{"disambiguationData":[OSD([subQ52])]});Q1=makeQuery(id+"F9.boolean.opBoolean","SPLIT",FACE,{"disambiguationData":[TD([subQ1])],"derivedFrom":makeQuery(id+"F6.boolean.opBoolean","MERGE",FACE,{"derivedFrom":[makeQuery(id+"FuSGAjuN3hY24FW_1.boolean.opBoolean","SPLIT",FACE,{"disambiguationData":[TD([subQ63])],"derivedFrom":makeQuery(id+"F3.boolean.opBoolean","SPLIT",FACE,{"disambiguationData":[TD([subQ63])],"derivedFrom":subQ53})}),makeQuery(id+"F3.boolean.opBoolean","SPLIT",FACE,{"disambiguationData":[TD([subQ1])],"derivedFrom":subQ53})],"fromTools":[makeQuery(id+"F6.opExtrude","CAP_FACE",FACE,{"disambiguationData":[OSD([sQuery(id+"F5.wireOp",EDGE,"E58.bottom"),sQuery(id+"F5.wireOp",EDGE,"E58.top"),sQuery(id+"F5.wireOp",EDGE,"E58.left"),sQuery(id+"F5.wireOp",EDGE,"E58.right")])],"isStart":false}),makeQuery(id+"F6.opExtrude","CAP_FACE",FACE,{"disambiguationData":[OSD([sQuery(id+"F5.wireOp",EDGE,"TwUVh8Jm-KBbL-sydY-1FMm-F6mmMaZqGzpT.bottom"),sQuery(id+"F5.wireOp",EDGE,"TwUVh8Jm-KBbL-sydY-1FMm-F6mmMaZqGzpT.top"),sQuery(id+"F5.wireOp",EDGE,"TwUVh8Jm-KBbL-sydY-1FMm-F6mmMaZqGzpT.left"),sQuery(id+"F5.wireOp",EDGE,"TwUVh8Jm-KBbL-sydY-1FMm-F6mmMaZqGzpT.right")])],"isStart":false}),makeQuery(id+"F6.opExtrude","CAP_FACE",FACE,{"disambiguationData":[OSD([sQuery(id+"F5.wireOp",EDGE,"12a840b2-8adb-4d60-9d90-1feae7f4b4320.MirrorCS"),sQuery(id+"F5.wireOp",EDGE,"12a840b2-8adb-4d60-9d90-1feae7f4b4321.MirrorCS"),sQuery(id+"F5.wireOp",EDGE,"12a840b2-8adb-4d60-9d90-1feae7f4b4323.MirrorCS"),sQuery(id+"F5.wireOp",EDGE,"12a840b2-8adb-4d60-9d90-1feae7f4b4324.MirrorCS")])],"isStart":false})]})});}
            var Q2;
            {var subQ0=sQuery(id+"F0.wireOp",EDGE,"E7.MirrorC");var subQ1=makeQuery(id+"F1.opExtrude","SWEPT_FACE",FACE,{"disambiguationData":[OSD([subQ0])]});var subQ2=sQuery(id+"F0.wireOp",EDGE,"E38.MirrorCS");var subQ3=sQuery(id+"F0.wireOp",EDGE,"E37.MirrorCS");var subQ4=sQuery(id+"F0.wireOp",EDGE,"E35.MirrorCS");var subQ5=sQuery(id+"F0.wireOp",EDGE,"E34.right");var subQ6=sQuery(id+"F0.wireOp",EDGE,"E34.left");var subQ7=sQuery(id+"F0.wireOp",EDGE,"E34.top");var subQ8=sQuery(id+"F0.wireOp",EDGE,"E28.left");var subQ9=sQuery(id+"F0.wireOp",EDGE,"E34.bottom");var subQ10=sQuery(id+"F0.wireOp",EDGE,"E28.top");var subQ11=sQuery(id+"F0.wireOp",EDGE,"E33.MirrorC");var subQ12=sQuery(id+"F0.wireOp",EDGE,"E32.MirrorC");var subQ13=sQuery(id+"F0.wireOp",EDGE,"E31.MirrorC");var subQ14=sQuery(id+"F0.wireOp",EDGE,"E30");var subQ15=sQuery(id+"F0.wireOp",EDGE,"E24.MirrorCS");var subQ16=sQuery(id+"F0.wireOp",EDGE,"E29.right");var subQ17=sQuery(id+"F0.wireOp",EDGE,"E23.MirrorCS");var subQ18=sQuery(id+"F0.wireOp",EDGE,"E29.left");var subQ19=sQuery(id+"F0.wireOp",EDGE,"E22.MirrorCS");var subQ20=sQuery(id+"F0.wireOp",EDGE,"E29.top");var subQ21=sQuery(id+"F0.wireOp",EDGE,"E21.MirrorCS");var subQ22=sQuery(id+"F0.wireOp",EDGE,"E29.bottom");var subQ23=sQuery(id+"F0.wireOp",EDGE,"E28.right");var subQ24=sQuery(id+"F0.wireOp",EDGE,"E13.MirrorC");var subQ25=sQuery(id+"F0.wireOp",EDGE,"E17.top");var subQ26=sQuery(id+"F0.wireOp",EDGE,"E12.MirrorC");var subQ27=sQuery(id+"F0.wireOp",EDGE,"E17.bottom");var subQ28=sQuery(id+"F0.wireOp",EDGE,"E11.MirrorC");var subQ29=sQuery(id+"F0.wireOp",EDGE,"E28.bottom");var subQ30=sQuery(id+"F0.wireOp",EDGE,"E10");var subQ31=sQuery(id+"F0.wireOp",EDGE,"E26.MirrorCS");var subQ32=sQuery(id+"F0.wireOp",EDGE,"E36.MirrorCS");var subQ33=sQuery(id+"F0.wireOp",EDGE,"E6");var subQ34=sQuery(id+"F0.wireOp",EDGE,"E19");var subQ35=sQuery(id+"F0.wireOp",EDGE,"E9.MirrorC");var subQ36=sQuery(id+"F0.wireOp",EDGE,"E25.MirrorCS");var subQ37=sQuery(id+"F0.wireOp",EDGE,"E8.MirrorC");var subQ38=sQuery(id+"F0.wireOp",EDGE,"E17.left");var subQ39=sQuery(id+"F0.wireOp",EDGE,"E17.right");var subQ40=sQuery(id+"F0.wireOp",EDGE,"E18");var subQ41=sQuery(id+"F0.wireOp",EDGE,"E40.trimOffspring");var subQ42=sQuery(id+"F0.wireOp",EDGE,"E39.trimOffspring");var subQ43=sQuery(id+"F0.wireOp",EDGE,"faqvqiBR-mRV4-xvH0-xbDX-PeENiLaSJtV9");var subQ44=sQuery(id+"F0.wireOp",EDGE,"2JwCXgoE-gSOf-8Eer-RTGS-hlqyIdlCKONg");var subQ45=sQuery(id+"F0.wireOp",EDGE,"E16.trimOffspring");var subQ46=sQuery(id+"F0.wireOp",EDGE,"E15.right");var subQ47=sQuery(id+"F0.wireOp",EDGE,"E15.left");var subQ48=sQuery(id+"F0.wireOp",EDGE,"E15.top");var subQ49=sQuery(id+"F0.wireOp",EDGE,"E14.right");var subQ50=sQuery(id+"F0.wireOp",EDGE,"E14.left");var subQ51=sQuery(id+"F0.wireOp",EDGE,"E14.top");var subQ52=sQuery(id+"F0.wireOp",EDGE,"E14.bottom");var subQ53=makeQuery(id+"F1.opExtrude","CAP_FACE",FACE,{"disambiguationData":[OSD([subQ33,subQ0,subQ37,subQ35,subQ30,subQ28,subQ26,subQ24,subQ52,subQ51,subQ50,subQ49,subQ48,subQ47,subQ46,subQ45,subQ27,subQ25,subQ38,subQ39,subQ40,subQ34,subQ21,subQ19,subQ17,subQ15,subQ36,subQ31,subQ29,subQ10,subQ8,subQ23,subQ22,subQ20,subQ18,subQ16,subQ14,subQ13,subQ12,subQ11,subQ9,subQ7,subQ6,subQ5,subQ4,subQ32,subQ3,subQ2,subQ44,subQ43,subQ42,subQ41])],"isStart":false});var subQ63=makeQuery(id+"F1.opExtrude","SWEPT_FACE",FACE,{"disambiguationData":[OSD([subQ52])]});Q2=makeQuery(id+"F9.boolean.opBoolean","SPLIT",FACE,{"disambiguationData":[TD([subQ1])],"derivedFrom":makeQuery(id+"F6.boolean.opBoolean","MERGE",FACE,{"derivedFrom":[makeQuery(id+"FuSGAjuN3hY24FW_1.boolean.opBoolean","SPLIT",FACE,{"disambiguationData":[TD([subQ63])],"derivedFrom":makeQuery(id+"F3.boolean.opBoolean","SPLIT",FACE,{"disambiguationData":[TD([subQ63])],"derivedFrom":subQ53})}),makeQuery(id+"F3.boolean.opBoolean","SPLIT",FACE,{"disambiguationData":[TD([makeQuery(id+"F1.opExtrude","SWEPT_FACE",FACE,{"disambiguationData":[OSD([subQ33])]})])],"derivedFrom":subQ53})],"fromTools":[makeQuery(id+"F6.opExtrude","CAP_FACE",FACE,{"disambiguationData":[OSD([sQuery(id+"F5.wireOp",EDGE,"E58.bottom"),sQuery(id+"F5.wireOp",EDGE,"E58.top"),sQuery(id+"F5.wireOp",EDGE,"E58.left"),sQuery(id+"F5.wireOp",EDGE,"E58.right")])],"isStart":false}),makeQuery(id+"F6.opExtrude","CAP_FACE",FACE,{"disambiguationData":[OSD([sQuery(id+"F5.wireOp",EDGE,"TwUVh8Jm-KBbL-sydY-1FMm-F6mmMaZqGzpT.bottom"),sQuery(id+"F5.wireOp",EDGE,"TwUVh8Jm-KBbL-sydY-1FMm-F6mmMaZqGzpT.top"),sQuery(id+"F5.wireOp",EDGE,"TwUVh8Jm-KBbL-sydY-1FMm-F6mmMaZqGzpT.left"),sQuery(id+"F5.wireOp",EDGE,"TwUVh8Jm-KBbL-sydY-1FMm-F6mmMaZqGzpT.right")])],"isStart":false}),makeQuery(id+"F6.opExtrude","CAP_FACE",FACE,{"disambiguationData":[OSD([sQuery(id+"F5.wireOp",EDGE,"12a840b2-8adb-4d60-9d90-1feae7f4b4320.MirrorCS"),sQuery(id+"F5.wireOp",EDGE,"12a840b2-8adb-4d60-9d90-1feae7f4b4321.MirrorCS"),sQuery(id+"F5.wireOp",EDGE,"12a840b2-8adb-4d60-9d90-1feae7f4b4323.MirrorCS"),sQuery(id+"F5.wireOp",EDGE,"12a840b2-8adb-4d60-9d90-1feae7f4b4324.MirrorCS")])],"isStart":false})]})});}
            var Q3;
            {var subQ0=sQuery(id+"F0.wireOp",EDGE,"E8.MirrorC");var subQ1=makeQuery(id+"F1.opExtrude","SWEPT_FACE",FACE,{"disambiguationData":[OSD([subQ0])]});var subQ2=sQuery(id+"F0.wireOp",EDGE,"E38.MirrorCS");var subQ3=sQuery(id+"F0.wireOp",EDGE,"E37.MirrorCS");var subQ4=sQuery(id+"F0.wireOp",EDGE,"E35.MirrorCS");var subQ5=sQuery(id+"F0.wireOp",EDGE,"E34.right");var subQ6=sQuery(id+"F0.wireOp",EDGE,"E34.left");var subQ7=sQuery(id+"F0.wireOp",EDGE,"E34.top");var subQ8=sQuery(id+"F0.wireOp",EDGE,"E28.left");var subQ9=sQuery(id+"F0.wireOp",EDGE,"E34.bottom");var subQ10=sQuery(id+"F0.wireOp",EDGE,"E28.top");var subQ11=sQuery(id+"F0.wireOp",EDGE,"E33.MirrorC");var subQ12=sQuery(id+"F0.wireOp",EDGE,"E32.MirrorC");var subQ13=sQuery(id+"F0.wireOp",EDGE,"E31.MirrorC");var subQ14=sQuery(id+"F0.wireOp",EDGE,"E30");var subQ15=sQuery(id+"F0.wireOp",EDGE,"E24.MirrorCS");var subQ16=sQuery(id+"F0.wireOp",EDGE,"E29.right");var subQ17=sQuery(id+"F0.wireOp",EDGE,"E23.MirrorCS");var subQ18=sQuery(id+"F0.wireOp",EDGE,"E29.left");var subQ19=sQuery(id+"F0.wireOp",EDGE,"E22.MirrorCS");var subQ20=sQuery(id+"F0.wireOp",EDGE,"E29.top");var subQ21=sQuery(id+"F0.wireOp",EDGE,"E21.MirrorCS");var subQ22=sQuery(id+"F0.wireOp",EDGE,"E29.bottom");var subQ23=sQuery(id+"F0.wireOp",EDGE,"E28.right");var subQ24=sQuery(id+"F0.wireOp",EDGE,"E13.MirrorC");var subQ25=sQuery(id+"F0.wireOp",EDGE,"E17.top");var subQ26=sQuery(id+"F0.wireOp",EDGE,"E12.MirrorC");var subQ27=sQuery(id+"F0.wireOp",EDGE,"E17.bottom");var subQ28=sQuery(id+"F0.wireOp",EDGE,"E11.MirrorC");var subQ29=sQuery(id+"F0.wireOp",EDGE,"E28.bottom");var subQ30=sQuery(id+"F0.wireOp",EDGE,"E10");var subQ31=sQuery(id+"F0.wireOp",EDGE,"E26.MirrorCS");var subQ32=sQuery(id+"F0.wireOp",EDGE,"E36.MirrorCS");var subQ33=sQuery(id+"F0.wireOp",EDGE,"E6");var subQ34=sQuery(id+"F0.wireOp",EDGE,"E19");var subQ35=sQuery(id+"F0.wireOp",EDGE,"E9.MirrorC");var subQ36=sQuery(id+"F0.wireOp",EDGE,"E25.MirrorCS");var subQ37=sQuery(id+"F0.wireOp",EDGE,"E7.MirrorC");var subQ38=sQuery(id+"F0.wireOp",EDGE,"E17.left");var subQ39=sQuery(id+"F0.wireOp",EDGE,"E17.right");var subQ40=sQuery(id+"F0.wireOp",EDGE,"E18");var subQ41=sQuery(id+"F0.wireOp",EDGE,"E40.trimOffspring");var subQ42=sQuery(id+"F0.wireOp",EDGE,"E39.trimOffspring");var subQ43=sQuery(id+"F0.wireOp",EDGE,"faqvqiBR-mRV4-xvH0-xbDX-PeENiLaSJtV9");var subQ44=sQuery(id+"F0.wireOp",EDGE,"2JwCXgoE-gSOf-8Eer-RTGS-hlqyIdlCKONg");var subQ45=sQuery(id+"F0.wireOp",EDGE,"E16.trimOffspring");var subQ46=sQuery(id+"F0.wireOp",EDGE,"E15.right");var subQ47=sQuery(id+"F0.wireOp",EDGE,"E15.left");var subQ48=sQuery(id+"F0.wireOp",EDGE,"E15.top");var subQ49=sQuery(id+"F0.wireOp",EDGE,"E14.right");var subQ50=sQuery(id+"F0.wireOp",EDGE,"E14.left");var subQ51=sQuery(id+"F0.wireOp",EDGE,"E14.top");var subQ52=sQuery(id+"F0.wireOp",EDGE,"E14.bottom");var subQ53=makeQuery(id+"F1.opExtrude","CAP_FACE",FACE,{"disambiguationData":[OSD([subQ33,subQ37,subQ0,subQ35,subQ30,subQ28,subQ26,subQ24,subQ52,subQ51,subQ50,subQ49,subQ48,subQ47,subQ46,subQ45,subQ27,subQ25,subQ38,subQ39,subQ40,subQ34,subQ21,subQ19,subQ17,subQ15,subQ36,subQ31,subQ29,subQ10,subQ8,subQ23,subQ22,subQ20,subQ18,subQ16,subQ14,subQ13,subQ12,subQ11,subQ9,subQ7,subQ6,subQ5,subQ4,subQ32,subQ3,subQ2,subQ44,subQ43,subQ42,subQ41])],"isStart":false});var subQ63=makeQuery(id+"F1.opExtrude","SWEPT_FACE",FACE,{"disambiguationData":[OSD([subQ52])]});Q3=makeQuery(id+"F9.boolean.opBoolean","SPLIT",FACE,{"disambiguationData":[TD([subQ1])],"derivedFrom":makeQuery(id+"F6.boolean.opBoolean","MERGE",FACE,{"derivedFrom":[makeQuery(id+"FuSGAjuN3hY24FW_1.boolean.opBoolean","SPLIT",FACE,{"disambiguationData":[TD([subQ63])],"derivedFrom":makeQuery(id+"F3.boolean.opBoolean","SPLIT",FACE,{"disambiguationData":[TD([subQ63])],"derivedFrom":subQ53})}),makeQuery(id+"F3.boolean.opBoolean","SPLIT",FACE,{"disambiguationData":[TD([makeQuery(id+"F1.opExtrude","SWEPT_FACE",FACE,{"disambiguationData":[OSD([subQ33])]})])],"derivedFrom":subQ53})],"fromTools":[makeQuery(id+"F6.opExtrude","CAP_FACE",FACE,{"disambiguationData":[OSD([sQuery(id+"F5.wireOp",EDGE,"E58.bottom"),sQuery(id+"F5.wireOp",EDGE,"E58.top"),sQuery(id+"F5.wireOp",EDGE,"E58.left"),sQuery(id+"F5.wireOp",EDGE,"E58.right")])],"isStart":false}),makeQuery(id+"F6.opExtrude","CAP_FACE",FACE,{"disambiguationData":[OSD([sQuery(id+"F5.wireOp",EDGE,"TwUVh8Jm-KBbL-sydY-1FMm-F6mmMaZqGzpT.bottom"),sQuery(id+"F5.wireOp",EDGE,"TwUVh8Jm-KBbL-sydY-1FMm-F6mmMaZqGzpT.top"),sQuery(id+"F5.wireOp",EDGE,"TwUVh8Jm-KBbL-sydY-1FMm-F6mmMaZqGzpT.left"),sQuery(id+"F5.wireOp",EDGE,"TwUVh8Jm-KBbL-sydY-1FMm-F6mmMaZqGzpT.right")])],"isStart":false}),makeQuery(id+"F6.opExtrude","CAP_FACE",FACE,{"disambiguationData":[OSD([sQuery(id+"F5.wireOp",EDGE,"12a840b2-8adb-4d60-9d90-1feae7f4b4320.MirrorCS"),sQuery(id+"F5.wireOp",EDGE,"12a840b2-8adb-4d60-9d90-1feae7f4b4321.MirrorCS"),sQuery(id+"F5.wireOp",EDGE,"12a840b2-8adb-4d60-9d90-1feae7f4b4323.MirrorCS"),sQuery(id+"F5.wireOp",EDGE,"12a840b2-8adb-4d60-9d90-1feae7f4b4324.MirrorCS")])],"isStart":false})]})});}
            extrude(context, id + "F20", {"entities" : qUnion([Q0, Q1, Q2, Q3]), "operationType" : NewBodyOperationType.REMOVE, "oppositeDirection" : true, "depth" : 0.5 * mm, "offsetDistance" : 25 * mm});
        }
        {
            var Q0;
            {var subQ0=sQuery(id+"F0.wireOp",EDGE,"E17.right");var subQ1=sQuery(id+"F5.wireOp",EDGE,"E64.MirrorCS");var subQ2=sQuery(id+"F5.wireOp",EDGE,"E63.MirrorCS");var subQ3=sQuery(id+"F5.wireOp",EDGE,"E62.MirrorCS");var subQ4=sQuery(id+"F5.wireOp",EDGE,"E61.MirrorCS");var subQ5=sQuery(id+"F5.wireOp",EDGE,"E60.right");var subQ6=sQuery(id+"F5.wireOp",EDGE,"E60.left");var subQ7=sQuery(id+"F5.wireOp",EDGE,"E60.top");var subQ8=sQuery(id+"F5.wireOp",EDGE,"E60.bottom");var subQ9=sQuery(id+"F5.wireOp",EDGE,"12a840b2-8adb-4d60-9d90-1feae7f4b4324.MirrorCS");var subQ10=sQuery(id+"F5.wireOp",EDGE,"12a840b2-8adb-4d60-9d90-1feae7f4b4323.MirrorCS");var subQ11=sQuery(id+"F5.wireOp",EDGE,"12a840b2-8adb-4d60-9d90-1feae7f4b4321.MirrorCS");var subQ12=sQuery(id+"F5.wireOp",EDGE,"12a840b2-8adb-4d60-9d90-1feae7f4b4320.MirrorCS");var subQ13=sQuery(id+"F5.wireOp",EDGE,"TwUVh8Jm-KBbL-sydY-1FMm-F6mmMaZqGzpT.right");var subQ14=sQuery(id+"F5.wireOp",EDGE,"TwUVh8Jm-KBbL-sydY-1FMm-F6mmMaZqGzpT.left");var subQ15=sQuery(id+"F5.wireOp",EDGE,"TwUVh8Jm-KBbL-sydY-1FMm-F6mmMaZqGzpT.top");var subQ16=sQuery(id+"F5.wireOp",EDGE,"TwUVh8Jm-KBbL-sydY-1FMm-F6mmMaZqGzpT.bottom");var subQ17=sQuery(id+"F5.wireOp",EDGE,"E59.right");var subQ18=sQuery(id+"F5.wireOp",EDGE,"E59.left");var subQ19=sQuery(id+"F5.wireOp",EDGE,"E59.top");var subQ20=sQuery(id+"F5.wireOp",EDGE,"E59.bottom");var subQ21=sQuery(id+"F5.wireOp",EDGE,"E58.right");var subQ22=sQuery(id+"F5.wireOp",EDGE,"E58.left");var subQ23=sQuery(id+"F5.wireOp",EDGE,"E58.top");var subQ24=sQuery(id+"F5.wireOp",EDGE,"E58.bottom");var subQ25=sQuery(id+"F0.wireOp",EDGE,"E45.MirrorCS");var subQ26=sQuery(id+"F0.wireOp",EDGE,"E44.MirrorCS");var subQ27=sQuery(id+"F0.wireOp",EDGE,"E43.trimOffspring");var subQ28=sQuery(id+"F0.wireOp",EDGE,"E42");var subQ29=sQuery(id+"F0.wireOp",EDGE,"E41");var subQ30=sQuery(id+"F0.wireOp",EDGE,"E40.trimOffspring");var subQ31=sQuery(id+"F0.wireOp",EDGE,"E39.trimOffspring");var subQ32=sQuery(id+"F0.wireOp",EDGE,"E38.MirrorCS");var subQ33=sQuery(id+"F0.wireOp",EDGE,"E37.MirrorCS");var subQ34=sQuery(id+"F0.wireOp",EDGE,"E36.MirrorCS");var subQ35=sQuery(id+"F0.wireOp",EDGE,"E35.MirrorCS");var subQ36=sQuery(id+"F0.wireOp",EDGE,"E34.right");var subQ37=sQuery(id+"F0.wireOp",EDGE,"E34.left");var subQ38=sQuery(id+"F0.wireOp",EDGE,"E34.top");var subQ39=sQuery(id+"F0.wireOp",EDGE,"E34.bottom");var subQ40=sQuery(id+"F0.wireOp",EDGE,"E33.MirrorC");var subQ41=sQuery(id+"F0.wireOp",EDGE,"E32.MirrorC");var subQ42=sQuery(id+"F0.wireOp",EDGE,"E31.MirrorC");var subQ43=sQuery(id+"F0.wireOp",EDGE,"E30");var subQ44=sQuery(id+"F0.wireOp",EDGE,"E29.right");var subQ45=sQuery(id+"F0.wireOp",EDGE,"E29.left");var subQ46=sQuery(id+"F0.wireOp",EDGE,"E29.top");var subQ47=sQuery(id+"F0.wireOp",EDGE,"E29.bottom");var subQ48=sQuery(id+"F0.wireOp",EDGE,"E28.right");var subQ49=sQuery(id+"F0.wireOp",EDGE,"E28.left");var subQ50=sQuery(id+"F0.wireOp",EDGE,"E28.top");var subQ51=sQuery(id+"F0.wireOp",EDGE,"E28.bottom");var subQ52=sQuery(id+"F0.wireOp",EDGE,"E26.MirrorCS");var subQ53=sQuery(id+"F0.wireOp",EDGE,"E25.MirrorCS");var subQ54=sQuery(id+"F0.wireOp",EDGE,"E24.MirrorCS");var subQ55=sQuery(id+"F0.wireOp",EDGE,"E23.MirrorCS");var subQ56=sQuery(id+"F0.wireOp",EDGE,"E22.MirrorCS");var subQ57=sQuery(id+"F0.wireOp",EDGE,"E21.MirrorCS");var subQ58=sQuery(id+"F0.wireOp",EDGE,"E19");var subQ59=sQuery(id+"F0.wireOp",EDGE,"E18");var subQ60=sQuery(id+"F0.wireOp",EDGE,"E17.left");var subQ61=sQuery(id+"F0.wireOp",EDGE,"E17.top");var subQ62=sQuery(id+"F0.wireOp",EDGE,"E17.bottom");var subQ63=sQuery(id+"F0.wireOp",EDGE,"E15.right");var subQ64=sQuery(id+"F0.wireOp",EDGE,"E15.left");var subQ65=sQuery(id+"F0.wireOp",EDGE,"E15.top");var subQ66=sQuery(id+"F0.wireOp",EDGE,"E14.right");var subQ67=sQuery(id+"F0.wireOp",EDGE,"E14.top");var subQ68=sQuery(id+"F0.wireOp",EDGE,"E13.MirrorC");var subQ69=sQuery(id+"F0.wireOp",EDGE,"E12.MirrorC");var subQ70=sQuery(id+"F0.wireOp",EDGE,"E11.MirrorC");var subQ71=sQuery(id+"F0.wireOp",EDGE,"E10");var subQ72=sQuery(id+"F0.wireOp",EDGE,"E9.MirrorC");var subQ73=sQuery(id+"F0.wireOp",EDGE,"E8.MirrorC");var subQ74=sQuery(id+"F0.wireOp",EDGE,"E7.MirrorC");var subQ75=sQuery(id+"F0.wireOp",EDGE,"E6");var subQ118=makeQuery(id+"F1.opExtrude","SWEPT_FACE",FACE,{"disambiguationData":[OSD([subQ71])]});var subQ139=makeQuery(id+"F1.opExtrude","CAP_FACE",FACE,{"disambiguationData":[OSD([subQ75,subQ74,subQ73,subQ72,subQ71,subQ70,subQ69,subQ68,subQ67,subQ66,subQ65,subQ64,subQ63,subQ62,subQ61,subQ60,subQ0,subQ59,subQ58,subQ57,subQ56,subQ55,subQ54,subQ53,subQ52,subQ51,subQ50,subQ49,subQ48,subQ47,subQ46,subQ45,subQ44,subQ43,subQ42,subQ41,subQ40,subQ39,subQ38,subQ37,subQ36,subQ35,subQ34,subQ33,subQ32,subQ31,subQ30,subQ29,subQ28,subQ27,subQ26,subQ25])],"isStart":false});Q0=makeQuery(id+"F15.boolean.opBoolean","MERGE",FACE,{"derivedFrom":[makeQuery(id+"F9.boolean.opBoolean","SPLIT",FACE,{"disambiguationData":[TD([subQ118])],"derivedFrom":makeQuery(id+"F7.boolean.opBoolean","MERGE",FACE,{"derivedFrom":[makeQuery(id+"F6.boolean.opBoolean","MERGE",FACE,{"derivedFrom":[makeQuery(id+"F3.boolean.opBoolean","SPLIT",FACE,{"disambiguationData":[TD([makeQuery(id+"F1.opExtrude","SWEPT_FACE",FACE,{"disambiguationData":[OSD([subQ67])]})])],"derivedFrom":subQ139}),makeQuery(id+"F3.boolean.opBoolean","SPLIT",FACE,{"disambiguationData":[TD([makeQuery(id+"F1.opExtrude","SWEPT_FACE",FACE,{"disambiguationData":[OSD([subQ75])]})])],"derivedFrom":subQ139})],"fromTools":[makeQuery(id+"F6.opExtrude","CAP_FACE",FACE,{"disambiguationData":[OSD([subQ24,subQ23,subQ22,subQ21])],"isStart":false}),makeQuery(id+"F6.opExtrude","CAP_FACE",FACE,{"disambiguationData":[OSD([subQ20,subQ19,subQ18,subQ17])],"isStart":false}),makeQuery(id+"F6.opExtrude","CAP_FACE",FACE,{"disambiguationData":[OSD([subQ16,subQ15,subQ14,subQ13])],"isStart":false}),makeQuery(id+"F6.opExtrude","CAP_FACE",FACE,{"disambiguationData":[OSD([subQ12,subQ11,subQ10,subQ9])],"isStart":false}),makeQuery(id+"F6.opExtrude","CAP_FACE",FACE,{"disambiguationData":[OSD([subQ8,subQ7,subQ6,subQ5])],"isStart":false}),makeQuery(id+"F6.opExtrude","CAP_FACE",FACE,{"disambiguationData":[OSD([subQ4,subQ3,subQ2,subQ1])],"isStart":false})]}),makeQuery(id+"F7.opExtrude","SWEPT_FACE",FACE,{"disambiguationData":[OSD([subQ67]),TDD([makeQuery(id+"F1.opExtrude","CAP_EDGE",EDGE,{"disambiguationData":[OSD([subQ67])],"isStart":false})])]})]})}),makeQuery(id+"F15.opExtrude","CAP_FACE",FACE,{"disambiguationData":[OSD([subQ75,subQ74,subQ73,subQ72,subQ71,subQ70,subQ69,subQ68,subQ67,subQ66,subQ65,subQ64,subQ63,subQ62,subQ61,subQ60,subQ0,subQ59,subQ58,subQ57,subQ56,subQ55,subQ54,subQ53,subQ52,subQ51,subQ50,subQ49,subQ48,subQ47,subQ46,subQ45,subQ44,subQ43,subQ42,subQ41,subQ40,subQ39,subQ38,subQ37,subQ36,subQ35,subQ34,subQ33,subQ32,subQ31,subQ30,subQ29,subQ28,subQ27,subQ26,subQ25,subQ24,subQ23,subQ22,subQ21,subQ20,subQ19,subQ18,subQ17,subQ16,subQ15,subQ14,subQ13,subQ12,subQ11,subQ10,subQ9,subQ8,subQ7,subQ6,subQ5,subQ4,subQ3,subQ2,subQ1,sQuery(id+"F14.wireOp",EDGE,"E89"),sQuery(id+"F14.wireOp",EDGE,"E90"),sQuery(id+"F14.wireOp",EDGE,"E91")])],"isStart":true}),makeQuery(id+"F15.opExtrude","CAP_FACE",FACE,{"disambiguationData":[OSD([subQ60,sQuery(id+"F14.wireOp",EDGE,"E92"),sQuery(id+"F14.wireOp",EDGE,"E93"),sQuery(id+"F14.wireOp",EDGE,"E94")])],"isStart":true}),makeQuery(id+"F15.opExtrude","CAP_FACE",FACE,{"disambiguationData":[OSD([subQ60,sQuery(id+"F14.wireOp",EDGE,"E95"),sQuery(id+"F14.wireOp",EDGE,"E96"),sQuery(id+"F14.wireOp",EDGE,"E97")])],"isStart":true}),makeQuery(id+"F15.opExtrude","CAP_FACE",FACE,{"disambiguationData":[OSD([subQ0,sQuery(id+"F14.wireOp",EDGE,"E98.MirrorCS"),sQuery(id+"F14.wireOp",EDGE,"E99.MirrorCS"),sQuery(id+"F14.wireOp",EDGE,"E106.MirrorCS")])],"isStart":true}),makeQuery(id+"F15.opExtrude","CAP_FACE",FACE,{"disambiguationData":[OSD([subQ75,subQ74,subQ73,subQ72,subQ71,subQ70,subQ69,subQ68,subQ67,subQ66,subQ65,subQ64,subQ63,subQ62,subQ61,subQ60,subQ0,subQ59,subQ58,subQ57,subQ56,subQ55,subQ54,subQ53,subQ52,subQ51,subQ50,subQ49,subQ48,subQ47,subQ46,subQ45,subQ44,subQ43,subQ42,subQ41,subQ40,subQ39,subQ38,subQ37,subQ36,subQ35,subQ34,subQ33,subQ32,subQ31,subQ30,subQ29,subQ28,subQ27,subQ26,subQ25,subQ24,subQ23,subQ22,subQ21,subQ20,subQ19,subQ18,subQ17,subQ16,subQ15,subQ14,subQ13,subQ12,subQ11,subQ10,subQ9,subQ8,subQ7,subQ6,subQ5,subQ4,subQ3,subQ2,subQ1,sQuery(id+"F14.wireOp",EDGE,"E100.MirrorCS"),sQuery(id+"F14.wireOp",EDGE,"E102.MirrorCS"),sQuery(id+"F14.wireOp",EDGE,"E105.MirrorCS")])],"isStart":true}),makeQuery(id+"F15.opExtrude","CAP_FACE",FACE,{"disambiguationData":[OSD([subQ0,sQuery(id+"F14.wireOp",EDGE,"E101.MirrorCS"),sQuery(id+"F14.wireOp",EDGE,"E103.MirrorCS"),sQuery(id+"F14.wireOp",EDGE,"E104.MirrorCS")])],"isStart":true})]});}
            var sketch = newSketch(context, id + "F21", { "sketchPlane" : qUnion([Q0])});
            skLineSegment(sketch, "E131", {"start": v(-6.7, -19.5) * mm, "end": v(-6.7, -17.1) * mm});
            skLineSegment(sketch, "E132", {"start": v(-6.7, -17.1) * mm, "end": v(-4.3, -17.1) * mm});
            skLineSegment(sketch, "E133", {"start": v(-4.3, -17.1) * mm, "end": v(-4.3, -19.5) * mm});
            skLineSegment(sketch, "E134", {"start": v(2.9, -19.5) * mm, "end": v(2.9, -17.1) * mm});
            skLineSegment(sketch, "E135", {"start": v(2.9, -17.1) * mm, "end": v(5.3, -17.1) * mm});
            skLineSegment(sketch, "E136", {"start": v(5.3, -17.1) * mm, "end": v(5.3, -19.5) * mm});
            skLineSegment(sketch, "E137", {"start": v(-6.7, -19.5) * mm, "end": v(-4.3, -19.5) * mm});
            skLineSegment(sketch, "E138", {"start": v(2.9, -19.5) * mm, "end": v(5.3, -19.5) * mm});
            skSolve(sketch);
        }
        {
            var Q0;
            Q0=makeQuery(id+"F21.imprint","IMPRINT",FACE,{"disambiguationData":[TD([[makeQuery(id+"F21.imprint","IMPRINT",EDGE,{"derivedFrom":sQuery(id+"F21.wireOp",EDGE,"E131")}),-1.0]])]});
            var Q1;
            Q1=makeQuery(id+"F21.imprint","IMPRINT",FACE,{"disambiguationData":[TD([[makeQuery(id+"F21.imprint","IMPRINT",EDGE,{"derivedFrom":sQuery(id+"F21.wireOp",EDGE,"E134")}),-1.0]])]});
            var Q2;
            {var subQ0=sQuery(id+"F0.wireOp",EDGE,"E17.right");var subQ1=sQuery(id+"F5.wireOp",EDGE,"E64.MirrorCS");var subQ2=sQuery(id+"F5.wireOp",EDGE,"E63.MirrorCS");var subQ3=sQuery(id+"F5.wireOp",EDGE,"E62.MirrorCS");var subQ4=sQuery(id+"F5.wireOp",EDGE,"E61.MirrorCS");var subQ5=sQuery(id+"F5.wireOp",EDGE,"E60.right");var subQ6=sQuery(id+"F5.wireOp",EDGE,"E60.left");var subQ7=sQuery(id+"F5.wireOp",EDGE,"E60.top");var subQ8=sQuery(id+"F5.wireOp",EDGE,"E60.bottom");var subQ9=sQuery(id+"F5.wireOp",EDGE,"12a840b2-8adb-4d60-9d90-1feae7f4b4324.MirrorCS");var subQ10=sQuery(id+"F5.wireOp",EDGE,"12a840b2-8adb-4d60-9d90-1feae7f4b4323.MirrorCS");var subQ11=sQuery(id+"F5.wireOp",EDGE,"12a840b2-8adb-4d60-9d90-1feae7f4b4321.MirrorCS");var subQ12=sQuery(id+"F5.wireOp",EDGE,"12a840b2-8adb-4d60-9d90-1feae7f4b4320.MirrorCS");var subQ13=sQuery(id+"F5.wireOp",EDGE,"TwUVh8Jm-KBbL-sydY-1FMm-F6mmMaZqGzpT.right");var subQ14=sQuery(id+"F5.wireOp",EDGE,"TwUVh8Jm-KBbL-sydY-1FMm-F6mmMaZqGzpT.left");var subQ15=sQuery(id+"F5.wireOp",EDGE,"TwUVh8Jm-KBbL-sydY-1FMm-F6mmMaZqGzpT.top");var subQ16=sQuery(id+"F5.wireOp",EDGE,"TwUVh8Jm-KBbL-sydY-1FMm-F6mmMaZqGzpT.bottom");var subQ17=sQuery(id+"F5.wireOp",EDGE,"E59.right");var subQ18=sQuery(id+"F5.wireOp",EDGE,"E59.left");var subQ19=sQuery(id+"F5.wireOp",EDGE,"E59.top");var subQ20=sQuery(id+"F5.wireOp",EDGE,"E59.bottom");var subQ21=sQuery(id+"F5.wireOp",EDGE,"E58.right");var subQ22=sQuery(id+"F5.wireOp",EDGE,"E58.left");var subQ23=sQuery(id+"F5.wireOp",EDGE,"E58.top");var subQ24=sQuery(id+"F5.wireOp",EDGE,"E58.bottom");var subQ25=sQuery(id+"F0.wireOp",EDGE,"E45.MirrorCS");var subQ26=sQuery(id+"F0.wireOp",EDGE,"E44.MirrorCS");var subQ27=sQuery(id+"F0.wireOp",EDGE,"E43.trimOffspring");var subQ28=sQuery(id+"F0.wireOp",EDGE,"E42");var subQ29=sQuery(id+"F0.wireOp",EDGE,"E41");var subQ30=sQuery(id+"F0.wireOp",EDGE,"E40.trimOffspring");var subQ31=sQuery(id+"F0.wireOp",EDGE,"E39.trimOffspring");var subQ32=sQuery(id+"F0.wireOp",EDGE,"E38.MirrorCS");var subQ33=sQuery(id+"F0.wireOp",EDGE,"E37.MirrorCS");var subQ34=sQuery(id+"F0.wireOp",EDGE,"E36.MirrorCS");var subQ35=sQuery(id+"F0.wireOp",EDGE,"E35.MirrorCS");var subQ36=sQuery(id+"F0.wireOp",EDGE,"E34.right");var subQ37=sQuery(id+"F0.wireOp",EDGE,"E34.left");var subQ38=sQuery(id+"F0.wireOp",EDGE,"E34.top");var subQ39=sQuery(id+"F0.wireOp",EDGE,"E34.bottom");var subQ40=sQuery(id+"F0.wireOp",EDGE,"E33.MirrorC");var subQ41=sQuery(id+"F0.wireOp",EDGE,"E32.MirrorC");var subQ42=sQuery(id+"F0.wireOp",EDGE,"E31.MirrorC");var subQ43=sQuery(id+"F0.wireOp",EDGE,"E30");var subQ44=sQuery(id+"F0.wireOp",EDGE,"E29.right");var subQ45=sQuery(id+"F0.wireOp",EDGE,"E29.left");var subQ46=sQuery(id+"F0.wireOp",EDGE,"E29.top");var subQ47=sQuery(id+"F0.wireOp",EDGE,"E29.bottom");var subQ48=sQuery(id+"F0.wireOp",EDGE,"E28.right");var subQ49=sQuery(id+"F0.wireOp",EDGE,"E28.left");var subQ50=sQuery(id+"F0.wireOp",EDGE,"E28.top");var subQ51=sQuery(id+"F0.wireOp",EDGE,"E28.bottom");var subQ52=sQuery(id+"F0.wireOp",EDGE,"E26.MirrorCS");var subQ53=sQuery(id+"F0.wireOp",EDGE,"E25.MirrorCS");var subQ54=sQuery(id+"F0.wireOp",EDGE,"E24.MirrorCS");var subQ55=sQuery(id+"F0.wireOp",EDGE,"E23.MirrorCS");var subQ56=sQuery(id+"F0.wireOp",EDGE,"E22.MirrorCS");var subQ57=sQuery(id+"F0.wireOp",EDGE,"E21.MirrorCS");var subQ58=sQuery(id+"F0.wireOp",EDGE,"E19");var subQ59=sQuery(id+"F0.wireOp",EDGE,"E18");var subQ60=sQuery(id+"F0.wireOp",EDGE,"E17.left");var subQ61=sQuery(id+"F0.wireOp",EDGE,"E17.top");var subQ62=sQuery(id+"F0.wireOp",EDGE,"E17.bottom");var subQ63=sQuery(id+"F0.wireOp",EDGE,"E15.right");var subQ64=sQuery(id+"F0.wireOp",EDGE,"E15.left");var subQ65=sQuery(id+"F0.wireOp",EDGE,"E15.top");var subQ66=sQuery(id+"F0.wireOp",EDGE,"E14.right");var subQ67=sQuery(id+"F0.wireOp",EDGE,"E14.top");var subQ68=sQuery(id+"F0.wireOp",EDGE,"E13.MirrorC");var subQ69=sQuery(id+"F0.wireOp",EDGE,"E12.MirrorC");var subQ70=sQuery(id+"F0.wireOp",EDGE,"E11.MirrorC");var subQ71=sQuery(id+"F0.wireOp",EDGE,"E10");var subQ72=sQuery(id+"F0.wireOp",EDGE,"E9.MirrorC");var subQ73=sQuery(id+"F0.wireOp",EDGE,"E8.MirrorC");var subQ74=sQuery(id+"F0.wireOp",EDGE,"E7.MirrorC");var subQ75=sQuery(id+"F0.wireOp",EDGE,"E6");Q2=makeQuery(id+"F17.boolean.opBoolean","MERGE",FACE,{"derivedFrom":[makeQuery(id+"F15.boolean.opBoolean","MERGE",FACE,{"derivedFrom":[makeQuery(id+"F7.boolean.opBoolean","MERGE",FACE,{"derivedFrom":[makeQuery(id+"F1.opExtrude","CAP_FACE",FACE,{"disambiguationData":[OSD([subQ75,subQ74,subQ73,subQ72,subQ71,subQ70,subQ69,subQ68,subQ67,subQ66,subQ65,subQ64,subQ63,subQ62,subQ61,subQ60,subQ0,subQ59,subQ58,subQ57,subQ56,subQ55,subQ54,subQ53,subQ52,subQ51,subQ50,subQ49,subQ48,subQ47,subQ46,subQ45,subQ44,subQ43,subQ42,subQ41,subQ40,subQ39,subQ38,subQ37,subQ36,subQ35,subQ34,subQ33,subQ32,subQ31,subQ30,subQ29,subQ28,subQ27,subQ26,subQ25])],"isStart":true}),makeQuery(id+"F7.opExtrude","SWEPT_FACE",FACE,{"disambiguationData":[OSD([subQ67]),TDD([makeQuery(id+"F1.opExtrude","CAP_EDGE",EDGE,{"disambiguationData":[OSD([subQ67])],"isStart":true})])]})]}),makeQuery(id+"F15.opExtrude","CAP_FACE",FACE,{"disambiguationData":[OSD([subQ75,subQ74,subQ73,subQ72,subQ71,subQ70,subQ69,subQ68,subQ67,subQ66,subQ65,subQ64,subQ63,subQ62,subQ61,subQ60,subQ0,subQ59,subQ58,subQ57,subQ56,subQ55,subQ54,subQ53,subQ52,subQ51,subQ50,subQ49,subQ48,subQ47,subQ46,subQ45,subQ44,subQ43,subQ42,subQ41,subQ40,subQ39,subQ38,subQ37,subQ36,subQ35,subQ34,subQ33,subQ32,subQ31,subQ30,subQ29,subQ28,subQ27,subQ26,subQ25,subQ24,subQ23,subQ22,subQ21,subQ20,subQ19,subQ18,subQ17,subQ16,subQ15,subQ14,subQ13,subQ12,subQ11,subQ10,subQ9,subQ8,subQ7,subQ6,subQ5,subQ4,subQ3,subQ2,subQ1,sQuery(id+"F14.wireOp",EDGE,"E89"),sQuery(id+"F14.wireOp",EDGE,"E90"),sQuery(id+"F14.wireOp",EDGE,"E91")])],"isStart":false}),makeQuery(id+"F15.opExtrude","CAP_FACE",FACE,{"disambiguationData":[OSD([subQ60,sQuery(id+"F14.wireOp",EDGE,"E92"),sQuery(id+"F14.wireOp",EDGE,"E93"),sQuery(id+"F14.wireOp",EDGE,"E94")])],"isStart":false}),makeQuery(id+"F15.opExtrude","CAP_FACE",FACE,{"disambiguationData":[OSD([subQ60,sQuery(id+"F14.wireOp",EDGE,"E95"),sQuery(id+"F14.wireOp",EDGE,"E96"),sQuery(id+"F14.wireOp",EDGE,"E97")])],"isStart":false}),makeQuery(id+"F15.opExtrude","CAP_FACE",FACE,{"disambiguationData":[OSD([subQ0,sQuery(id+"F14.wireOp",EDGE,"E98.MirrorCS"),sQuery(id+"F14.wireOp",EDGE,"E99.MirrorCS"),sQuery(id+"F14.wireOp",EDGE,"E106.MirrorCS")])],"isStart":false}),makeQuery(id+"F15.opExtrude","CAP_FACE",FACE,{"disambiguationData":[OSD([subQ75,subQ74,subQ73,subQ72,subQ71,subQ70,subQ69,subQ68,subQ67,subQ66,subQ65,subQ64,subQ63,subQ62,subQ61,subQ60,subQ0,subQ59,subQ58,subQ57,subQ56,subQ55,subQ54,subQ53,subQ52,subQ51,subQ50,subQ49,subQ48,subQ47,subQ46,subQ45,subQ44,subQ43,subQ42,subQ41,subQ40,subQ39,subQ38,subQ37,subQ36,subQ35,subQ34,subQ33,subQ32,subQ31,subQ30,subQ29,subQ28,subQ27,subQ26,subQ25,subQ24,subQ23,subQ22,subQ21,subQ20,subQ19,subQ18,subQ17,subQ16,subQ15,subQ14,subQ13,subQ12,subQ11,subQ10,subQ9,subQ8,subQ7,subQ6,subQ5,subQ4,subQ3,subQ2,subQ1,sQuery(id+"F14.wireOp",EDGE,"E100.MirrorCS"),sQuery(id+"F14.wireOp",EDGE,"E102.MirrorCS"),sQuery(id+"F14.wireOp",EDGE,"E105.MirrorCS")])],"isStart":false}),makeQuery(id+"F15.opExtrude","CAP_FACE",FACE,{"disambiguationData":[OSD([subQ0,sQuery(id+"F14.wireOp",EDGE,"E101.MirrorCS"),sQuery(id+"F14.wireOp",EDGE,"E103.MirrorCS"),sQuery(id+"F14.wireOp",EDGE,"E104.MirrorCS")])],"isStart":false})]}),makeQuery(id+"F17.opExtrude","CAP_FACE",FACE,{"disambiguationData":[OSD([sQuery(id+"F16.wireOp",EDGE,"E107"),sQuery(id+"F16.wireOp",EDGE,"E108")])],"isStart":true}),makeQuery(id+"F17.opExtrude","CAP_FACE",FACE,{"disambiguationData":[OSD([sQuery(id+"F16.wireOp",EDGE,"E109.MirrorC"),sQuery(id+"F16.wireOp",EDGE,"E110.MirrorC")])],"isStart":true}),makeQuery(id+"F17.opExtrude","CAP_FACE",FACE,{"disambiguationData":[OSD([sQuery(id+"F16.wireOp",EDGE,"E111.MirrorC"),sQuery(id+"F16.wireOp",EDGE,"E113.MirrorC")])],"isStart":true}),makeQuery(id+"F17.opExtrude","CAP_FACE",FACE,{"disambiguationData":[OSD([sQuery(id+"F16.wireOp",EDGE,"E112.MirrorC"),sQuery(id+"F16.wireOp",EDGE,"E114.MirrorC")])],"isStart":true})]});}
            extrude(context, id + "F22", {"entities" : qUnion([Q0, Q1]), "operationType" : NewBodyOperationType.ADD, "endBound" : BoundingType.UP_TO_SURFACE, "oppositeDirection" : true, "depth" : 25 * mm, "endBoundEntityFace" : qUnion([Q2]), "offsetDistance" : 25 * mm});
        }
        {
            var Q0;
            {var subQ0=sQuery(id+"F14.wireOp",EDGE,"E103.MirrorCS");var subQ3=sQuery(id+"F0.wireOp",EDGE,"E38.MirrorCS");var subQ5=sQuery(id+"F0.wireOp",EDGE,"E35.MirrorCS");var subQ7=sQuery(id+"F14.wireOp",EDGE,"E102.MirrorCS");var subQ9=sQuery(id+"F0.wireOp",EDGE,"E34.right");var subQ11=sQuery(id+"F14.wireOp",EDGE,"E101.MirrorCS");var subQ13=sQuery(id+"F0.wireOp",EDGE,"E34.bottom");var subQ15=sQuery(id+"F14.wireOp",EDGE,"E92");var subQ16=sQuery(id+"F0.wireOp",EDGE,"E22.MirrorCS");var subQ18=sQuery(id+"F14.wireOp",EDGE,"E91");var subQ19=sQuery(id+"F14.wireOp",EDGE,"E90");var subQ20=sQuery(id+"F0.wireOp",EDGE,"E19");var subQ22=sQuery(id+"F0.wireOp",EDGE,"E17.right");var subQ23=sQuery(id+"F0.wireOp",EDGE,"E24.MirrorCS");var subQ24=sQuery(id+"F0.wireOp",EDGE,"E17.left");var subQ29=sQuery(id+"F14.wireOp",EDGE,"E100.MirrorCS");var subQ30=sQuery(id+"F0.wireOp",EDGE,"E31.MirrorC");var subQ34=sQuery(id+"F5.wireOp",EDGE,"E62.MirrorCS");var subQ36=sQuery(id+"F14.wireOp",EDGE,"E99.MirrorCS");var subQ37=sQuery(id+"F0.wireOp",EDGE,"E30");var subQ40=sQuery(id+"F0.wireOp",EDGE,"E14.top");var subQ42=sQuery(id+"F5.wireOp",EDGE,"E61.MirrorCS");var subQ44=sQuery(id+"F5.wireOp",EDGE,"E60.top");var subQ46=sQuery(id+"F5.wireOp",EDGE,"E60.bottom");var subQ48=sQuery(id+"F14.wireOp",EDGE,"E98.MirrorCS");var subQ50=sQuery(id+"F0.wireOp",EDGE,"E29.top");var subQ52=sQuery(id+"F5.wireOp",EDGE,"12a840b2-8adb-4d60-9d90-1feae7f4b4321.MirrorCS");var subQ54=sQuery(id+"F14.wireOp",EDGE,"E97");var subQ56=sQuery(id+"F0.wireOp",EDGE,"E29.bottom");var subQ58=sQuery(id+"F5.wireOp",EDGE,"12a840b2-8adb-4d60-9d90-1feae7f4b4320.MirrorCS");var subQ60=sQuery(id+"F14.wireOp",EDGE,"E96");var subQ62=sQuery(id+"F0.wireOp",EDGE,"E28.right");var subQ64=sQuery(id+"F5.wireOp",EDGE,"TwUVh8Jm-KBbL-sydY-1FMm-F6mmMaZqGzpT.top");var subQ66=sQuery(id+"F5.wireOp",EDGE,"TwUVh8Jm-KBbL-sydY-1FMm-F6mmMaZqGzpT.bottom");var subQ68=sQuery(id+"F5.wireOp",EDGE,"E59.right");var subQ70=sQuery(id+"F14.wireOp",EDGE,"E95");var subQ72=sQuery(id+"F0.wireOp",EDGE,"E28.bottom");var subQ74=sQuery(id+"F5.wireOp",EDGE,"E59.left");var subQ76=sQuery(id+"F14.wireOp",EDGE,"E94");var subQ77=sQuery(id+"F0.wireOp",EDGE,"E26.MirrorCS");var subQ79=sQuery(id+"F5.wireOp",EDGE,"E58.right");var subQ81=sQuery(id+"F14.wireOp",EDGE,"E93");var subQ82=sQuery(id+"F5.wireOp",EDGE,"E58.left");var subQ84=sQuery(id+"F0.wireOp",EDGE,"E34.left");var subQ86=sQuery(id+"F0.wireOp",EDGE,"E45.MirrorCS");var subQ88=sQuery(id+"F0.wireOp",EDGE,"E29.left");var subQ96=sQuery(id+"F0.wireOp",EDGE,"E13.MirrorC");var subQ101=sQuery(id+"F14.wireOp",EDGE,"E106.MirrorCS");var subQ103=sQuery(id+"F0.wireOp",EDGE,"E12.MirrorC");var subQ107=sQuery(id+"F14.wireOp",EDGE,"E105.MirrorCS");var subQ108=sQuery(id+"F0.wireOp",EDGE,"E11.MirrorC");var subQ110=sQuery(id+"F0.wireOp",EDGE,"E10");var subQ111=makeQuery(id+"F1.opExtrude","SWEPT_FACE",FACE,{"disambiguationData":[OSD([subQ110])]});var subQ113=sQuery(id+"F14.wireOp",EDGE,"E89");var subQ114=sQuery(id+"F0.wireOp",EDGE,"E14.right");var subQ116=sQuery(id+"F0.wireOp",EDGE,"E15.top");var subQ118=sQuery(id+"F0.wireOp",EDGE,"E42");var subQ119=sQuery(id+"F0.wireOp",EDGE,"E39.trimOffspring");var subQ120=sQuery(id+"F0.wireOp",EDGE,"E15.left");var subQ122=sQuery(id+"F0.wireOp",EDGE,"E44.MirrorCS");var subQ123=sQuery(id+"F0.wireOp",EDGE,"E40.trimOffspring");var subQ124=sQuery(id+"F0.wireOp",EDGE,"E15.right");var subQ126=sQuery(id+"F0.wireOp",EDGE,"E17.bottom");var subQ128=sQuery(id+"F0.wireOp",EDGE,"E29.right");var subQ132=sQuery(id+"F0.wireOp",EDGE,"E36.MirrorCS");var subQ135=sQuery(id+"F14.wireOp",EDGE,"E104.MirrorCS");var subQ136=sQuery(id+"F0.wireOp",EDGE,"E32.MirrorC");var subQ139=sQuery(id+"F0.wireOp",EDGE,"E33.MirrorC");var subQ142=sQuery(id+"F0.wireOp",EDGE,"E28.top");var subQ145=sQuery(id+"F0.wireOp",EDGE,"E43.trimOffspring");var subQ147=sQuery(id+"F0.wireOp",EDGE,"E28.left");var subQ152=sQuery(id+"F0.wireOp",EDGE,"E41");var subQ154=sQuery(id+"F5.wireOp",EDGE,"E64.MirrorCS");var subQ155=sQuery(id+"F5.wireOp",EDGE,"E63.MirrorCS");var subQ156=sQuery(id+"F5.wireOp",EDGE,"E60.right");var subQ157=sQuery(id+"F5.wireOp",EDGE,"E60.left");var subQ158=sQuery(id+"F5.wireOp",EDGE,"12a840b2-8adb-4d60-9d90-1feae7f4b4324.MirrorCS");var subQ159=sQuery(id+"F5.wireOp",EDGE,"12a840b2-8adb-4d60-9d90-1feae7f4b4323.MirrorCS");var subQ160=sQuery(id+"F5.wireOp",EDGE,"TwUVh8Jm-KBbL-sydY-1FMm-F6mmMaZqGzpT.right");var subQ161=sQuery(id+"F5.wireOp",EDGE,"TwUVh8Jm-KBbL-sydY-1FMm-F6mmMaZqGzpT.left");var subQ162=sQuery(id+"F5.wireOp",EDGE,"E59.top");var subQ163=sQuery(id+"F5.wireOp",EDGE,"E59.bottom");var subQ164=sQuery(id+"F5.wireOp",EDGE,"E58.top");var subQ165=sQuery(id+"F5.wireOp",EDGE,"E58.bottom");var subQ166=sQuery(id+"F0.wireOp",EDGE,"E37.MirrorCS");var subQ167=sQuery(id+"F0.wireOp",EDGE,"E34.top");var subQ168=sQuery(id+"F0.wireOp",EDGE,"E25.MirrorCS");var subQ169=sQuery(id+"F0.wireOp",EDGE,"E23.MirrorCS");var subQ170=sQuery(id+"F0.wireOp",EDGE,"E21.MirrorCS");var subQ171=sQuery(id+"F0.wireOp",EDGE,"E18");var subQ172=sQuery(id+"F0.wireOp",EDGE,"E17.top");var subQ173=sQuery(id+"F0.wireOp",EDGE,"E9.MirrorC");var subQ174=sQuery(id+"F0.wireOp",EDGE,"E8.MirrorC");var subQ175=sQuery(id+"F0.wireOp",EDGE,"E7.MirrorC");var subQ176=sQuery(id+"F0.wireOp",EDGE,"E6");var subQ182=makeQuery(id+"F1.opExtrude","CAP_FACE",FACE,{"disambiguationData":[OSD([subQ176,subQ175,subQ174,subQ173,subQ110,subQ108,subQ103,subQ96,subQ40,subQ114,subQ116,subQ120,subQ124,subQ126,subQ172,subQ24,subQ22,subQ171,subQ20,subQ170,subQ16,subQ169,subQ23,subQ168,subQ77,subQ72,subQ142,subQ147,subQ62,subQ56,subQ50,subQ88,subQ128,subQ37,subQ30,subQ136,subQ139,subQ13,subQ167,subQ84,subQ9,subQ5,subQ132,subQ166,subQ3,subQ119,subQ123,subQ152,subQ118,subQ145,subQ122,subQ86])],"isStart":false});Q0=makeQuery(id+"F22.boolean.opBoolean","MERGE",FACE,{"derivedFrom":[makeQuery(id+"F19.boolean.opBoolean","SPLIT",FACE,{"disambiguationData":[TD([subQ111])],"derivedFrom":makeQuery(id+"F15.boolean.opBoolean","MERGE",FACE,{"derivedFrom":[makeQuery(id+"F9.boolean.opBoolean","SPLIT",FACE,{"disambiguationData":[TD([subQ111])],"derivedFrom":makeQuery(id+"F7.boolean.opBoolean","MERGE",FACE,{"derivedFrom":[makeQuery(id+"F6.boolean.opBoolean","MERGE",FACE,{"derivedFrom":[makeQuery(id+"F3.boolean.opBoolean","SPLIT",FACE,{"disambiguationData":[TD([makeQuery(id+"F1.opExtrude","SWEPT_FACE",FACE,{"disambiguationData":[OSD([subQ40])]})])],"derivedFrom":subQ182}),makeQuery(id+"F3.boolean.opBoolean","SPLIT",FACE,{"disambiguationData":[TD([makeQuery(id+"F1.opExtrude","SWEPT_FACE",FACE,{"disambiguationData":[OSD([subQ176])]})])],"derivedFrom":subQ182})],"fromTools":[makeQuery(id+"F6.opExtrude","CAP_FACE",FACE,{"disambiguationData":[OSD([subQ165,subQ164,subQ82,subQ79])],"isStart":false}),makeQuery(id+"F6.opExtrude","CAP_FACE",FACE,{"disambiguationData":[OSD([subQ163,subQ162,subQ74,subQ68])],"isStart":false}),makeQuery(id+"F6.opExtrude","CAP_FACE",FACE,{"disambiguationData":[OSD([subQ66,subQ64,subQ161,subQ160])],"isStart":false}),makeQuery(id+"F6.opExtrude","CAP_FACE",FACE,{"disambiguationData":[OSD([subQ58,subQ52,subQ159,subQ158])],"isStart":false}),makeQuery(id+"F6.opExtrude","CAP_FACE",FACE,{"disambiguationData":[OSD([subQ46,subQ44,subQ157,subQ156])],"isStart":false}),makeQuery(id+"F6.opExtrude","CAP_FACE",FACE,{"disambiguationData":[OSD([subQ42,subQ34,subQ155,subQ154])],"isStart":false})]}),makeQuery(id+"F7.opExtrude","SWEPT_FACE",FACE,{"disambiguationData":[OSD([subQ40]),TDD([makeQuery(id+"F1.opExtrude","CAP_EDGE",EDGE,{"disambiguationData":[OSD([subQ40])],"isStart":false})])]})]})}),makeQuery(id+"F15.opExtrude","CAP_FACE",FACE,{"disambiguationData":[OSD([subQ176,subQ175,subQ174,subQ173,subQ110,subQ108,subQ103,subQ96,subQ40,subQ114,subQ116,subQ120,subQ124,subQ126,subQ172,subQ24,subQ22,subQ171,subQ20,subQ170,subQ16,subQ169,subQ23,subQ168,subQ77,subQ72,subQ142,subQ147,subQ62,subQ56,subQ50,subQ88,subQ128,subQ37,subQ30,subQ136,subQ139,subQ13,subQ167,subQ84,subQ9,subQ5,subQ132,subQ166,subQ3,subQ119,subQ123,subQ152,subQ118,subQ145,subQ122,subQ86,subQ165,subQ164,subQ82,subQ79,subQ163,subQ162,subQ74,subQ68,subQ66,subQ64,subQ161,subQ160,subQ58,subQ52,subQ159,subQ158,subQ46,subQ44,subQ157,subQ156,subQ42,subQ34,subQ155,subQ154,subQ113,subQ19,subQ18])],"isStart":true}),makeQuery(id+"F15.opExtrude","CAP_FACE",FACE,{"disambiguationData":[OSD([subQ24,subQ15,subQ81,subQ76])],"isStart":true}),makeQuery(id+"F15.opExtrude","CAP_FACE",FACE,{"disambiguationData":[OSD([subQ24,subQ70,subQ60,subQ54])],"isStart":true}),makeQuery(id+"F15.opExtrude","CAP_FACE",FACE,{"disambiguationData":[OSD([subQ22,subQ48,subQ36,subQ101])],"isStart":true}),makeQuery(id+"F15.opExtrude","CAP_FACE",FACE,{"disambiguationData":[OSD([subQ176,subQ175,subQ174,subQ173,subQ110,subQ108,subQ103,subQ96,subQ40,subQ114,subQ116,subQ120,subQ124,subQ126,subQ172,subQ24,subQ22,subQ171,subQ20,subQ170,subQ16,subQ169,subQ23,subQ168,subQ77,subQ72,subQ142,subQ147,subQ62,subQ56,subQ50,subQ88,subQ128,subQ37,subQ30,subQ136,subQ139,subQ13,subQ167,subQ84,subQ9,subQ5,subQ132,subQ166,subQ3,subQ119,subQ123,subQ152,subQ118,subQ145,subQ122,subQ86,subQ165,subQ164,subQ82,subQ79,subQ163,subQ162,subQ74,subQ68,subQ66,subQ64,subQ161,subQ160,subQ58,subQ52,subQ159,subQ158,subQ46,subQ44,subQ157,subQ156,subQ42,subQ34,subQ155,subQ154,subQ29,subQ7,subQ107])],"isStart":true}),makeQuery(id+"F15.opExtrude","CAP_FACE",FACE,{"disambiguationData":[OSD([subQ22,subQ11,subQ0,subQ135])],"isStart":true})]})}),makeQuery(id+"F22.opExtrude","CAP_FACE",FACE,{"disambiguationData":[OSD([sQuery(id+"F21.wireOp",EDGE,"E131"),sQuery(id+"F21.wireOp",EDGE,"E132"),sQuery(id+"F21.wireOp",EDGE,"E133"),sQuery(id+"F21.wireOp",EDGE,"E137")])],"isStart":true}),makeQuery(id+"F22.opExtrude","CAP_FACE",FACE,{"disambiguationData":[OSD([sQuery(id+"F21.wireOp",EDGE,"E134"),sQuery(id+"F21.wireOp",EDGE,"E135"),sQuery(id+"F21.wireOp",EDGE,"E136"),sQuery(id+"F21.wireOp",EDGE,"E138")])],"isStart":true})]});}
            var sketch = newSketch(context, id + "F23", { "sketchPlane" : qUnion([Q0])});
            skLineSegment(sketch, "E139.bottom", {"start": v(-4.3, -19.5) * mm, "end": v(2.9, -19.5) * mm});
            skLineSegment(sketch, "E139.top", {"start": v(-4.3, -20.8) * mm, "end": v(2.9, -20.8) * mm});
            skLineSegment(sketch, "E139.left", {"start": v(-4.3, -19.5) * mm, "end": v(-4.3, -20.8) * mm});
            skLineSegment(sketch, "E139.right", {"start": v(2.9, -19.5) * mm, "end": v(2.9, -20.8) * mm});
            skSolve(sketch);
        }
        {
            var Q0;
            Q0=makeQuery(id+"F23.imprint","IMPRINT",FACE,{"disambiguationData":[TD([[makeQuery(id+"F23.imprint","IMPRINT",EDGE,{"derivedFrom":sQuery(id+"F23.wireOp",EDGE,"E139.bottom")}),-1.0]])]});
            extrude(context, id + "F24", {"entities" : qUnion([Q0]), "operationType" : NewBodyOperationType.REMOVE, "oppositeDirection" : true, "depth" : 25 * mm, "offsetDistance" : 25 * mm});
        }
    });
